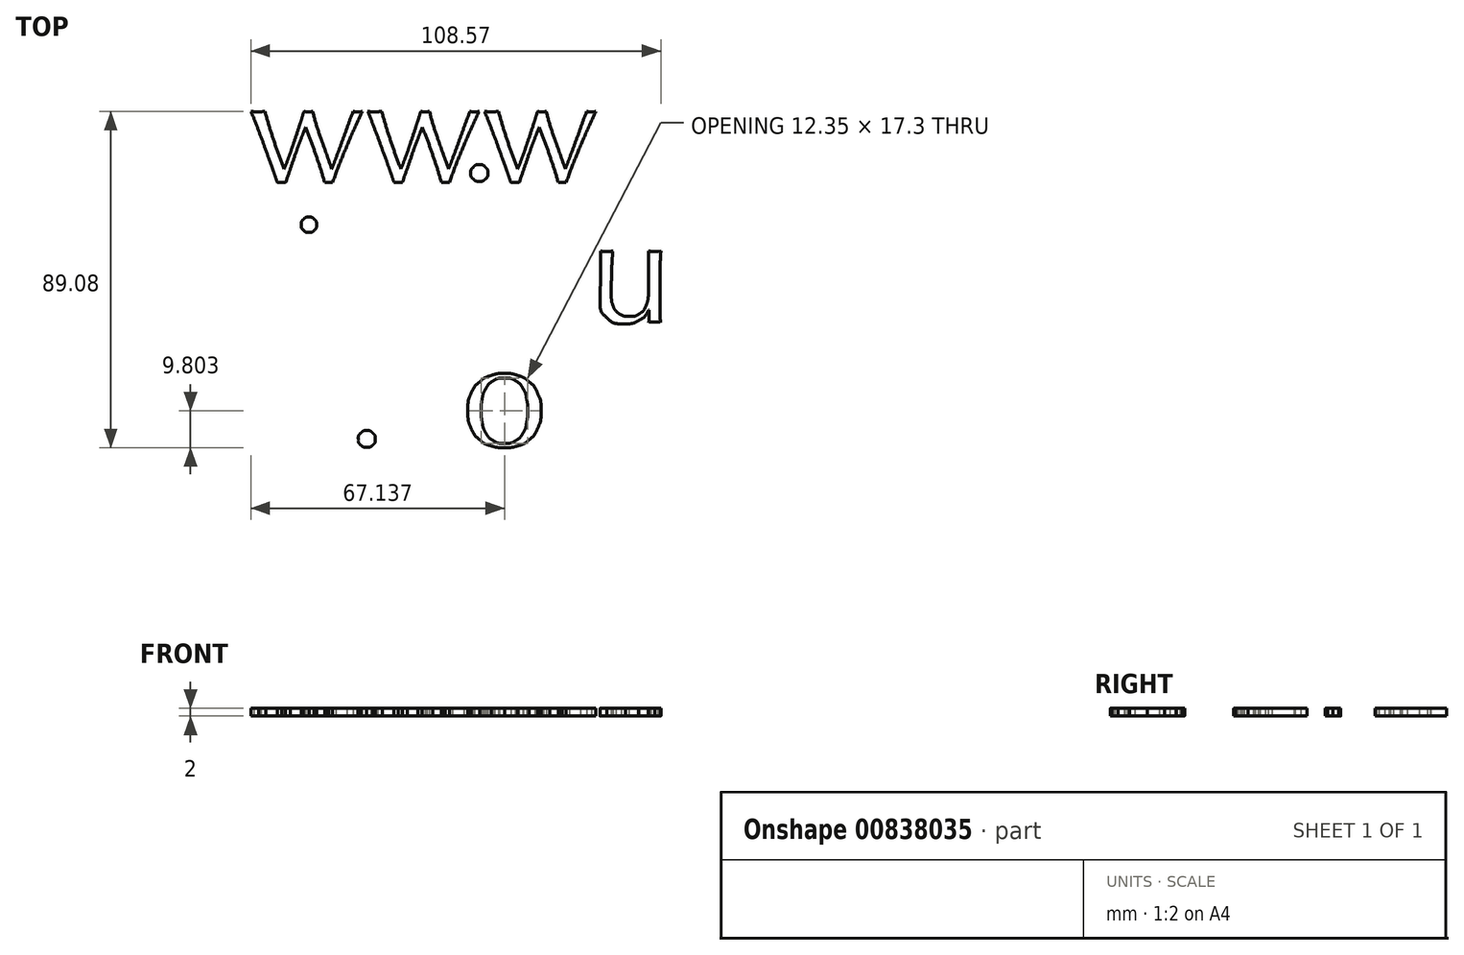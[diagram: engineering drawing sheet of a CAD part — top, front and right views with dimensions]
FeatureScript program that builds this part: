
annotation { "Feature Type Name" : "Feature", "Feature Type Description" : "" }
export const myFeature = defineFeature(function(context is Context, id is Id, definition is map)
    precondition{}
    {
        {
            var Q0;
            Q0=qCreatedBy(makeId("Top.planeOp"),FACE);
            var sketch = newSketch(context, id + "F0", { "sketchPlane" : qUnion([Q0])});
            skLineSegment(sketch, "E0", {"start": v(-60.09, 7.53) * mm, "end": v(-60.57, 7.53) * mm});
            skLineSegment(sketch, "E1", {"start": v(-60.57, 7.53) * mm, "end": v(-60.09, 7.53) * mm});
            skLineSegment(sketch, "E2", {"start": v(-51.53, 19.18) * mm, "end": v(-51.06, 19.18) * mm});
            skLineSegment(sketch, "E3", {"start": v(-51.06, 19.18) * mm, "end": v(-51.53, 19.18) * mm});
            skLineSegment(sketch, "E4", {"start": v(-41, 28.06) * mm, "end": v(-44.3, 26.66) * mm});
            skLineSegment(sketch, "E5", {"start": v(-44.3, 26.66) * mm, "end": v(-41, 28.06) * mm});
            skLineSegment(sketch, "E6", {"start": v(-45.34, 20.7) * mm, "end": v(-44.07, 20.7) * mm});
            skLineSegment(sketch, "E7", {"start": v(-44.07, 20.7) * mm, "end": v(-45.34, 20.7) * mm});
            skLineSegment(sketch, "E8", {"start": v(-36.39, 3.9) * mm, "end": v(-36.39, 4.86) * mm});
            skLineSegment(sketch, "E9", {"start": v(-36.39, 4.86) * mm, "end": v(-36.39, 3.9) * mm});
            skLineSegment(sketch, "E10", {"start": v(-41.12, 20.7) * mm, "end": v(-39.17, 20.7) * mm});
            skLineSegment(sketch, "E11", {"start": v(-39.17, 20.7) * mm, "end": v(-41.12, 20.7) * mm});
            skLineSegment(sketch, "E12", {"start": v(-36.95, 21.02) * mm, "end": v(-36.95, 21.45) * mm});
            skLineSegment(sketch, "E13", {"start": v(-36.95, 21.45) * mm, "end": v(-36.95, 21.85) * mm});
            skLineSegment(sketch, "E14", {"start": v(-36.95, 21.85) * mm, "end": v(-36.95, 21.02) * mm});
            skLineSegment(sketch, "E15", {"start": v(-40.8, 28.06) * mm, "end": v(-41, 28.06) * mm});
            skLineSegment(sketch, "E16", {"start": v(-41, 28.06) * mm, "end": v(-40.8, 28.06) * mm});
            skLineSegment(sketch, "E17", {"start": v(-32.28, 15.29) * mm, "end": v(-32.28, 11.15) * mm});
            skLineSegment(sketch, "E18", {"start": v(-32.28, 11.15) * mm, "end": v(-32.28, 15.29) * mm});
            skLineSegment(sketch, "E19", {"start": v(-29.34, 11.15) * mm, "end": v(-29.34, 15.29) * mm});
            skLineSegment(sketch, "E20", {"start": v(-29.34, 15.29) * mm, "end": v(-29.34, 11.15) * mm});
            skLineSegment(sketch, "E21", {"start": v(-21.25, 22.37) * mm, "end": v(-21.25, 15.17) * mm});
            skLineSegment(sketch, "E22", {"start": v(-21.25, 15.17) * mm, "end": v(-21.25, 22.37) * mm});
            skLineSegment(sketch, "E23", {"start": v(-18.3, 15.17) * mm, "end": v(-18.3, 22.37) * mm});
            skLineSegment(sketch, "E24", {"start": v(-18.3, 22.37) * mm, "end": v(-18.3, 15.17) * mm});
            skLineSegment(sketch, "E25", {"start": v(-10.13, 22.37) * mm, "end": v(-10.13, 15.17) * mm});
            skLineSegment(sketch, "E26", {"start": v(-10.13, 15.17) * mm, "end": v(-10.13, 22.37) * mm});
            skLineSegment(sketch, "E27", {"start": v(-7.19, 15.17) * mm, "end": v(-7.19, 22.37) * mm});
            skLineSegment(sketch, "E28", {"start": v(-7.19, 22.37) * mm, "end": v(-7.19, 15.17) * mm});
            skLineSegment(sketch, "E29", {"start": v(10.17, 13.73) * mm, "end": v(10, 7.77) * mm});
            skLineSegment(sketch, "E30", {"start": v(10, 7.77) * mm, "end": v(10.17, 13.73) * mm});
            skLineSegment(sketch, "E31", {"start": v(0.34, 20.82) * mm, "end": v(0.34, 18.75) * mm});
            skLineSegment(sketch, "E32", {"start": v(0.34, 18.75) * mm, "end": v(0.78, 18.75) * mm});
            skLineSegment(sketch, "E33", {"start": v(0.78, 18.75) * mm, "end": v(0.34, 20.82) * mm});
            skLineSegment(sketch, "E34", {"start": v(15.42, 4.3) * mm, "end": v(15.42, 5.18) * mm});
            skLineSegment(sketch, "E35", {"start": v(15.42, 5.18) * mm, "end": v(15.42, 4.3) * mm});
            skLineSegment(sketch, "E36", {"start": v(19.56, 7.53) * mm, "end": v(19.08, 7.53) * mm});
            skLineSegment(sketch, "E37", {"start": v(19.08, 7.53) * mm, "end": v(19.56, 7.53) * mm});
            skLineSegment(sketch, "E38", {"start": v(28.11, 19.18) * mm, "end": v(28.6, 19.18) * mm});
            skLineSegment(sketch, "E39", {"start": v(28.6, 19.18) * mm, "end": v(28.11, 19.18) * mm});
            skLineSegment(sketch, "E40", {"start": v(38.64, 28.06) * mm, "end": v(35.34, 26.66) * mm});
            skLineSegment(sketch, "E41", {"start": v(35.34, 26.66) * mm, "end": v(38.64, 28.06) * mm});
            skLineSegment(sketch, "E42", {"start": v(34.3, 20.7) * mm, "end": v(35.58, 20.7) * mm});
            skLineSegment(sketch, "E43", {"start": v(35.58, 20.7) * mm, "end": v(34.3, 20.7) * mm});
            skLineSegment(sketch, "E44", {"start": v(43.26, 3.9) * mm, "end": v(43.26, 4.86) * mm});
            skLineSegment(sketch, "E45", {"start": v(43.26, 4.86) * mm, "end": v(43.26, 3.9) * mm});
            skLineSegment(sketch, "E46", {"start": v(38.52, 20.7) * mm, "end": v(40.47, 20.7) * mm});
            skLineSegment(sketch, "E47", {"start": v(40.47, 20.7) * mm, "end": v(38.52, 20.7) * mm});
            skLineSegment(sketch, "E48", {"start": v(42.7, 21.02) * mm, "end": v(42.7, 21.45) * mm});
            skLineSegment(sketch, "E49", {"start": v(42.7, 21.45) * mm, "end": v(42.7, 21.85) * mm});
            skLineSegment(sketch, "E50", {"start": v(42.7, 21.85) * mm, "end": v(42.7, 21.02) * mm});
            skLineSegment(sketch, "E51", {"start": v(38.84, 28.06) * mm, "end": v(38.64, 28.06) * mm});
            skLineSegment(sketch, "E52", {"start": v(38.64, 28.06) * mm, "end": v(38.84, 28.06) * mm});
            skLineSegment(sketch, "E53", {"start": v(59.18, 7.13) * mm, "end": v(59.26, 7.13) * mm});
            skLineSegment(sketch, "E54", {"start": v(59.26, 7.13) * mm, "end": v(59.26, 5.42) * mm});
            skLineSegment(sketch, "E55", {"start": v(59.26, 5.42) * mm, "end": v(59.18, 7.13) * mm});
            skLineSegment(sketch, "E56", {"start": v(59.18, 19.54) * mm, "end": v(59.18, 16.2) * mm});
            skLineSegment(sketch, "E57", {"start": v(59.18, 16.2) * mm, "end": v(59.18, 19.54) * mm});
            skLineSegment(sketch, "E58", {"start": v(-50.25, -25.67) * mm, "end": v(-50.25, -28.1) * mm});
            skLineSegment(sketch, "E59", {"start": v(-50.25, -28.1) * mm, "end": v(-50.25, -25.67) * mm});
            skLineSegment(sketch, "E60", {"start": v(-47.3, -34.42) * mm, "end": v(-47.3, -31.84) * mm});
            skLineSegment(sketch, "E61", {"start": v(-47.3, -31.84) * mm, "end": v(-47.3, -34.42) * mm});
            skLineSegment(sketch, "E62", {"start": v(-59.88, -21.14) * mm, "end": v(-59.96, -21.14) * mm});
            skLineSegment(sketch, "E63", {"start": v(-59.96, -21.14) * mm, "end": v(-59.88, -21.14) * mm});
            skLineSegment(sketch, "E64", {"start": v(-62.9, -25.4) * mm, "end": v(-62.9, -29.53) * mm});
            skLineSegment(sketch, "E65", {"start": v(-62.9, -29.53) * mm, "end": v(-62.9, -25.4) * mm});
            skLineSegment(sketch, "E66", {"start": v(-59.96, -29.53) * mm, "end": v(-59.96, -26.15) * mm});
            skLineSegment(sketch, "E67", {"start": v(-59.96, -26.15) * mm, "end": v(-59.96, -29.53) * mm});
            skLineSegment(sketch, "E68", {"start": v(-27.55, -33.07) * mm, "end": v(-27.67, -36.85) * mm});
            skLineSegment(sketch, "E69", {"start": v(-27.67, -36.85) * mm, "end": v(-27.55, -33.07) * mm});
            skLineSegment(sketch, "E70", {"start": v(-27.67, -17.63) * mm, "end": v(-27.67, -21.53) * mm});
            skLineSegment(sketch, "E71", {"start": v(-27.67, -21.53) * mm, "end": v(-27.75, -21.53) * mm});
            skLineSegment(sketch, "E72", {"start": v(-27.75, -21.53) * mm, "end": v(-27.67, -17.63) * mm});
            skLineSegment(sketch, "E73", {"start": v(-27.63, -33.07) * mm, "end": v(-27.55, -33.07) * mm});
            skLineSegment(sketch, "E74", {"start": v(-27.55, -33.07) * mm, "end": v(-27.63, -33.07) * mm});
            skLineSegment(sketch, "E75", {"start": v(8.25, -25.12) * mm, "end": v(8.05, -25) * mm});
            skLineSegment(sketch, "E76", {"start": v(8.05, -25) * mm, "end": v(8.25, -25.12) * mm});
            skLineSegment(sketch, "E77", {"start": v(7.05, -14.06) * mm, "end": v(7.37, -14.06) * mm});
            skLineSegment(sketch, "E78", {"start": v(7.37, -14.06) * mm, "end": v(7.05, -14.06) * mm});
            skLineSegment(sketch, "E79", {"start": v(35.17, -17.52) * mm, "end": v(35.17, -21.66) * mm});
            skLineSegment(sketch, "E80", {"start": v(35.17, -21.66) * mm, "end": v(35.17, -17.52) * mm});
            skLineSegment(sketch, "E81", {"start": v(38.1, -21.66) * mm, "end": v(38.1, -18.27) * mm});
            skLineSegment(sketch, "E82", {"start": v(38.1, -18.27) * mm, "end": v(38.1, -21.66) * mm});
            skLineSegment(sketch, "E83", {"start": v(49.97, -13.62) * mm, "end": v(49.89, -13.62) * mm});
            skLineSegment(sketch, "E84", {"start": v(49.89, -13.62) * mm, "end": v(49.97, -13.62) * mm});
            skLineSegment(sketch, "E85", {"start": v(38.19, -13.26) * mm, "end": v(38.1, -13.26) * mm});
            skLineSegment(sketch, "E86", {"start": v(38.1, -13.26) * mm, "end": v(38.19, -13.26) * mm});
            skFitSpline(sketch, "E87", {"points": [v(-39.2, 40.8) * mm, v(-38.88, 40.85) * mm, v(-38.5, 40.88) * mm, v(-38.08, 40.88) * mm]});
            skFitSpline(sketch, "E88", {"points": [v(-38.08, 40.88) * mm, v(-37.66, 40.88) * mm, v(-37.28, 40.85) * mm, v(-36.97, 40.8) * mm]});
            skFitSpline(sketch, "E89", {"points": [v(-36.97, 40.8) * mm, v(-36.6, 41.91) * mm, v(-36.17, 43.16) * mm, v(-35.7, 44.54) * mm]});
            skFitSpline(sketch, "E90", {"points": [v(-35.7, 44.54) * mm, v(-35.22, 45.94) * mm, v(-34.74, 47.32) * mm, v(-34.26, 48.67) * mm]});
            skFitSpline(sketch, "E91", {"points": [v(-34.26, 48.67) * mm, v(-33.78, 50.03) * mm, v(-33.32, 51.29) * mm, v(-32.87, 52.45) * mm]});
            skFitSpline(sketch, "E92", {"points": [v(-32.87, 52.45) * mm, v(-32.42, 53.65) * mm, v(-32.03, 54.64) * mm, v(-31.72, 55.44) * mm]});
            skFitSpline(sketch, "E93", {"points": [v(-31.72, 55.44) * mm, v(-30.65, 52.81) * mm, v(-29.71, 50.3) * mm, v(-28.9, 47.92) * mm]});
            skFitSpline(sketch, "E94", {"points": [v(-28.9, 47.92) * mm, v(-28.07, 45.53) * mm, v(-27.31, 43.16) * mm, v(-26.62, 40.8) * mm]});
            skFitSpline(sketch, "E95", {"points": [v(-26.62, 40.8) * mm, v(-26.49, 40.85) * mm, v(-26.33, 40.88) * mm, v(-26.15, 40.88) * mm]});
            skFitSpline(sketch, "E96", {"points": [v(-26.15, 40.88) * mm, v(-25.96, 40.88) * mm, v(-25.77, 40.88) * mm, v(-25.59, 40.88) * mm]});
            skFitSpline(sketch, "E97", {"points": [v(-25.59, 40.88) * mm, v(-25.2, 40.88) * mm, v(-24.85, 40.85) * mm, v(-24.55, 40.8) * mm]});
            skFitSpline(sketch, "E98", {"points": [v(-24.55, 40.8) * mm, v(-23.41, 43.93) * mm, v(-22.2, 47.06) * mm, v(-20.9, 50.19) * mm]});
            skFitSpline(sketch, "E99", {"points": [v(-20.9, 50.19) * mm, v(-19.57, 53.32) * mm, v(-18.15, 56.48) * mm, v(-16.64, 59.7) * mm]});
            skFitSpline(sketch, "E100", {"points": [v(-16.64, 59.7) * mm, v(-17.09, 59.56) * mm, v(-17.49, 59.5) * mm, v(-17.83, 59.5) * mm]});
            skFitSpline(sketch, "E101", {"points": [v(-17.83, 59.5) * mm, v(-18.15, 59.5) * mm, v(-18.57, 59.56) * mm, v(-19.1, 59.7) * mm]});
            skFitSpline(sketch, "E102", {"points": [v(-19.1, 59.7) * mm, v(-19.55, 58.45) * mm, v(-20.04, 57.1) * mm, v(-20.58, 55.68) * mm]});
            skFitSpline(sketch, "E103", {"points": [v(-20.58, 55.68) * mm, v(-21.08, 54.24) * mm, v(-21.58, 52.84) * mm, v(-22.09, 51.46) * mm]});
            skFitSpline(sketch, "E104", {"points": [v(-22.09, 51.46) * mm, v(-22.6, 50.1) * mm, v(-23.08, 48.8) * mm, v(-23.56, 47.56) * mm]});
            skFitSpline(sketch, "E105", {"points": [v(-23.56, 47.56) * mm, v(-24.01, 46.34) * mm, v(-24.4, 45.3) * mm, v(-24.75, 44.46) * mm]});
            skFitSpline(sketch, "E106", {"points": [v(-24.75, 44.46) * mm, v(-25.7, 47.1) * mm, v(-26.62, 49.67) * mm, v(-27.5, 52.13) * mm]});
            skFitSpline(sketch, "E107", {"points": [v(-27.5, 52.13) * mm, v(-28.37, 54.63) * mm, v(-29.14, 57.15) * mm, v(-29.8, 59.7) * mm]});
            skFitSpline(sketch, "E108", {"points": [v(-29.8, 59.7) * mm, v(-30.02, 59.64) * mm, v(-30.2, 59.59) * mm, v(-30.36, 59.53) * mm]});
            skFitSpline(sketch, "E109", {"points": [v(-30.36, 59.53) * mm, v(-30.52, 59.5) * mm, v(-30.7, 59.5) * mm, v(-30.92, 59.5) * mm]});
            skFitSpline(sketch, "E110", {"points": [v(-30.92, 59.5) * mm, v(-31.24, 59.5) * mm, v(-31.64, 59.56) * mm, v(-32.11, 59.7) * mm]});
            skFitSpline(sketch, "E111", {"points": [v(-32.11, 59.7) * mm, v(-32.48, 58.45) * mm, v(-32.9, 57.1) * mm, v(-33.39, 55.64) * mm]});
            skFitSpline(sketch, "E112", {"points": [v(-33.39, 55.64) * mm, v(-33.86, 54.18) * mm, v(-34.34, 52.74) * mm, v(-34.82, 51.34) * mm]});
            skFitSpline(sketch, "E113", {"points": [v(-34.82, 51.34) * mm, v(-35.3, 49.93) * mm, v(-35.76, 48.62) * mm, v(-36.21, 47.4) * mm]});
            skFitSpline(sketch, "E114", {"points": [v(-36.21, 47.4) * mm, v(-36.66, 46.18) * mm, v(-37.05, 45.2) * mm, v(-37.36, 44.46) * mm]});
            skFitSpline(sketch, "E115", {"points": [v(-37.36, 44.46) * mm, v(-38.4, 47.1) * mm, v(-39.34, 49.68) * mm, v(-40.19, 52.17) * mm]});
            skFitSpline(sketch, "E116", {"points": [v(-40.19, 52.17) * mm, v(-41.01, 54.7) * mm, v(-41.77, 57.2) * mm, v(-42.46, 59.7) * mm]});
            skFitSpline(sketch, "E117", {"points": [v(-42.46, 59.7) * mm, v(-42.8, 59.64) * mm, v(-43.12, 59.59) * mm, v(-43.41, 59.53) * mm]});
            skFitSpline(sketch, "E118", {"points": [v(-43.41, 59.53) * mm, v(-43.7, 59.5) * mm, v(-44, 59.5) * mm, v(-44.29, 59.5) * mm]});
            skFitSpline(sketch, "E119", {"points": [v(-44.29, 59.5) * mm, v(-44.6, 59.5) * mm, v(-44.92, 59.5) * mm, v(-45.24, 59.53) * mm]});
            skFitSpline(sketch, "E120", {"points": [v(-45.24, 59.53) * mm, v(-45.53, 59.59) * mm, v(-45.84, 59.64) * mm, v(-46.16, 59.7) * mm]});
            skFitSpline(sketch, "E121", {"points": [v(-46.16, 59.7) * mm, v(-45.5, 58.1) * mm, v(-44.83, 56.4) * mm, v(-44.17, 54.6) * mm]});
            skFitSpline(sketch, "E122", {"points": [v(-44.17, 54.6) * mm, v(-43.48, 52.82) * mm, v(-42.83, 51.07) * mm, v(-42.22, 49.35) * mm]});
            skFitSpline(sketch, "E123", {"points": [v(-42.22, 49.35) * mm, v(-41.58, 47.65) * mm, v(-41, 46.05) * mm, v(-40.47, 44.54) * mm]});
            skFitSpline(sketch, "E124", {"points": [v(-40.47, 44.54) * mm, v(-39.94, 43.02) * mm, v(-39.51, 41.78) * mm, v(-39.2, 40.8) * mm]});
            skFitSpline(sketch, "E125", {"points": [v(-8.27, 40.8) * mm, v(-7.95, 40.85) * mm, v(-7.58, 40.88) * mm, v(-7.15, 40.88) * mm]});
            skFitSpline(sketch, "E126", {"points": [v(-7.15, 40.88) * mm, v(-6.73, 40.88) * mm, v(-6.36, 40.85) * mm, v(-6.04, 40.8) * mm]});
            skFitSpline(sketch, "E127", {"points": [v(-6.04, 40.8) * mm, v(-5.67, 41.91) * mm, v(-5.24, 43.16) * mm, v(-4.77, 44.54) * mm]});
            skFitSpline(sketch, "E128", {"points": [v(-4.77, 44.54) * mm, v(-4.29, 45.94) * mm, v(-3.81, 47.32) * mm, v(-3.33, 48.67) * mm]});
            skFitSpline(sketch, "E129", {"points": [v(-3.33, 48.67) * mm, v(-2.86, 50.03) * mm, v(-2.4, 51.29) * mm, v(-1.94, 52.45) * mm]});
            skFitSpline(sketch, "E130", {"points": [v(-1.94, 52.45) * mm, v(-1.5, 53.65) * mm, v(-1.1, 54.64) * mm, v(-0.79, 55.44) * mm]});
            skFitSpline(sketch, "E131", {"points": [v(-0.79, 55.44) * mm, v(0.27, 52.81) * mm, v(1.21, 50.3) * mm, v(2.04, 47.92) * mm]});
            skFitSpline(sketch, "E132", {"points": [v(2.04, 47.92) * mm, v(2.86, 45.53) * mm, v(3.61, 43.16) * mm, v(4.3, 40.8) * mm]});
            skFitSpline(sketch, "E133", {"points": [v(4.3, 40.8) * mm, v(4.44, 40.85) * mm, v(4.6, 40.88) * mm, v(4.78, 40.88) * mm]});
            skFitSpline(sketch, "E134", {"points": [v(4.78, 40.88) * mm, v(4.97, 40.88) * mm, v(5.15, 40.88) * mm, v(5.34, 40.88) * mm]});
            skFitSpline(sketch, "E135", {"points": [v(5.34, 40.88) * mm, v(5.74, 40.88) * mm, v(6.08, 40.85) * mm, v(6.37, 40.8) * mm]});
            skFitSpline(sketch, "E136", {"points": [v(6.37, 40.8) * mm, v(7.51, 43.93) * mm, v(8.73, 47.06) * mm, v(10.03, 50.19) * mm]});
            skFitSpline(sketch, "E137", {"points": [v(10.03, 50.19) * mm, v(11.36, 53.32) * mm, v(12.78, 56.48) * mm, v(14.3, 59.7) * mm]});
            skFitSpline(sketch, "E138", {"points": [v(14.3, 59.7) * mm, v(13.84, 59.56) * mm, v(13.44, 59.5) * mm, v(13.1, 59.5) * mm]});
            skFitSpline(sketch, "E139", {"points": [v(13.1, 59.5) * mm, v(12.78, 59.5) * mm, v(12.35, 59.56) * mm, v(11.82, 59.7) * mm]});
            skFitSpline(sketch, "E140", {"points": [v(11.82, 59.7) * mm, v(11.37, 58.45) * mm, v(10.88, 57.1) * mm, v(10.35, 55.68) * mm]});
            skFitSpline(sketch, "E141", {"points": [v(10.35, 55.68) * mm, v(9.85, 54.24) * mm, v(9.34, 52.84) * mm, v(8.84, 51.46) * mm]});
            skFitSpline(sketch, "E142", {"points": [v(8.84, 51.46) * mm, v(8.34, 50.1) * mm, v(7.84, 48.8) * mm, v(7.37, 47.56) * mm]});
            skFitSpline(sketch, "E143", {"points": [v(7.37, 47.56) * mm, v(6.92, 46.34) * mm, v(6.52, 45.3) * mm, v(6.17, 44.46) * mm]});
            skFitSpline(sketch, "E144", {"points": [v(6.17, 44.46) * mm, v(5.22, 47.1) * mm, v(4.3, 49.67) * mm, v(3.43, 52.13) * mm]});
            skFitSpline(sketch, "E145", {"points": [v(3.43, 52.13) * mm, v(2.55, 54.63) * mm, v(1.78, 57.15) * mm, v(1.12, 59.7) * mm]});
            skFitSpline(sketch, "E146", {"points": [v(1.12, 59.7) * mm, v(0.9, 59.64) * mm, v(0.72, 59.59) * mm, v(0.56, 59.53) * mm]});
            skFitSpline(sketch, "E147", {"points": [v(0.56, 59.53) * mm, v(0.4, 59.5) * mm, v(0.22, 59.5) * mm, v(0, 59.5) * mm]});
            skFitSpline(sketch, "E148", {"points": [v(0, 59.5) * mm, v(-0.31, 59.5) * mm, v(-0.7, 59.56) * mm, v(-1.19, 59.7) * mm]});
            skFitSpline(sketch, "E149", {"points": [v(-1.19, 59.7) * mm, v(-1.56, 58.45) * mm, v(-1.98, 57.1) * mm, v(-2.46, 55.64) * mm]});
            skFitSpline(sketch, "E150", {"points": [v(-2.46, 55.64) * mm, v(-2.94, 54.18) * mm, v(-3.41, 52.74) * mm, v(-3.9, 51.34) * mm]});
            skFitSpline(sketch, "E151", {"points": [v(-3.9, 51.34) * mm, v(-4.37, 49.93) * mm, v(-4.83, 48.62) * mm, v(-5.28, 47.4) * mm]});
            skFitSpline(sketch, "E152", {"points": [v(-5.28, 47.4) * mm, v(-5.74, 46.18) * mm, v(-6.12, 45.2) * mm, v(-6.44, 44.46) * mm]});
            skFitSpline(sketch, "E153", {"points": [v(-6.44, 44.46) * mm, v(-7.47, 47.1) * mm, v(-8.41, 49.68) * mm, v(-9.26, 52.17) * mm]});
            skFitSpline(sketch, "E154", {"points": [v(-9.26, 52.17) * mm, v(-10.08, 54.7) * mm, v(-10.84, 57.2) * mm, v(-11.53, 59.7) * mm]});
            skFitSpline(sketch, "E155", {"points": [v(-11.53, 59.7) * mm, v(-11.88, 59.64) * mm, v(-12.2, 59.59) * mm, v(-12.49, 59.53) * mm]});
            skFitSpline(sketch, "E156", {"points": [v(-12.49, 59.53) * mm, v(-12.78, 59.5) * mm, v(-13.07, 59.5) * mm, v(-13.36, 59.5) * mm]});
            skFitSpline(sketch, "E157", {"points": [v(-13.36, 59.5) * mm, v(-13.68, 59.5) * mm, v(-14, 59.5) * mm, v(-14.32, 59.53) * mm]});
            skFitSpline(sketch, "E158", {"points": [v(-14.32, 59.53) * mm, v(-14.6, 59.59) * mm, v(-14.91, 59.64) * mm, v(-15.23, 59.7) * mm]});
            skFitSpline(sketch, "E159", {"points": [v(-15.23, 59.7) * mm, v(-14.57, 58.1) * mm, v(-13.9, 56.4) * mm, v(-13.24, 54.6) * mm]});
            skFitSpline(sketch, "E160", {"points": [v(-13.24, 54.6) * mm, v(-12.55, 52.82) * mm, v(-11.9, 51.07) * mm, v(-11.3, 49.35) * mm]});
            skFitSpline(sketch, "E161", {"points": [v(-11.3, 49.35) * mm, v(-10.66, 47.65) * mm, v(-10.07, 46.05) * mm, v(-9.54, 44.54) * mm]});
            skFitSpline(sketch, "E162", {"points": [v(-9.54, 44.54) * mm, v(-9.01, 43.02) * mm, v(-8.59, 41.78) * mm, v(-8.27, 40.8) * mm]});
            skFitSpline(sketch, "E163", {"points": [v(22.66, 40.8) * mm, v(22.98, 40.85) * mm, v(23.35, 40.88) * mm, v(23.77, 40.88) * mm]});
            skFitSpline(sketch, "E164", {"points": [v(23.77, 40.88) * mm, v(24.2, 40.88) * mm, v(24.57, 40.85) * mm, v(24.89, 40.8) * mm]});
            skFitSpline(sketch, "E165", {"points": [v(24.89, 40.8) * mm, v(25.26, 41.91) * mm, v(25.68, 43.16) * mm, v(26.16, 44.54) * mm]});
            skFitSpline(sketch, "E166", {"points": [v(26.16, 44.54) * mm, v(26.64, 45.94) * mm, v(27.11, 47.32) * mm, v(27.6, 48.67) * mm]});
            skFitSpline(sketch, "E167", {"points": [v(27.6, 48.67) * mm, v(28.07, 50.03) * mm, v(28.53, 51.29) * mm, v(28.98, 52.45) * mm]});
            skFitSpline(sketch, "E168", {"points": [v(28.98, 52.45) * mm, v(29.44, 53.65) * mm, v(29.82, 54.64) * mm, v(30.14, 55.44) * mm]});
            skFitSpline(sketch, "E169", {"points": [v(30.14, 55.44) * mm, v(31.2, 52.81) * mm, v(32.14, 50.3) * mm, v(32.96, 47.92) * mm]});
            skFitSpline(sketch, "E170", {"points": [v(32.96, 47.92) * mm, v(33.79, 45.53) * mm, v(34.54, 43.16) * mm, v(35.23, 40.8) * mm]});
            skFitSpline(sketch, "E171", {"points": [v(35.23, 40.8) * mm, v(35.36, 40.85) * mm, v(35.52, 40.88) * mm, v(35.7, 40.88) * mm]});
            skFitSpline(sketch, "E172", {"points": [v(35.7, 40.88) * mm, v(35.9, 40.88) * mm, v(36.08, 40.88) * mm, v(36.27, 40.88) * mm]});
            skFitSpline(sketch, "E173", {"points": [v(36.27, 40.88) * mm, v(36.66, 40.88) * mm, v(37, 40.85) * mm, v(37.3, 40.8) * mm]});
            skFitSpline(sketch, "E174", {"points": [v(37.3, 40.8) * mm, v(38.44, 43.93) * mm, v(39.66, 47.06) * mm, v(40.96, 50.19) * mm]});
            skFitSpline(sketch, "E175", {"points": [v(40.96, 50.19) * mm, v(42.29, 53.32) * mm, v(43.7, 56.48) * mm, v(45.22, 59.7) * mm]});
            skFitSpline(sketch, "E176", {"points": [v(45.22, 59.7) * mm, v(44.77, 59.56) * mm, v(44.37, 59.5) * mm, v(44.02, 59.5) * mm]});
            skFitSpline(sketch, "E177", {"points": [v(44.02, 59.5) * mm, v(43.7, 59.5) * mm, v(43.28, 59.56) * mm, v(42.75, 59.7) * mm]});
            skFitSpline(sketch, "E178", {"points": [v(42.75, 59.7) * mm, v(42.3, 58.45) * mm, v(41.8, 57.1) * mm, v(41.28, 55.68) * mm]});
            skFitSpline(sketch, "E179", {"points": [v(41.28, 55.68) * mm, v(40.77, 54.24) * mm, v(40.27, 52.84) * mm, v(39.77, 51.46) * mm]});
            skFitSpline(sketch, "E180", {"points": [v(39.77, 51.46) * mm, v(39.26, 50.1) * mm, v(38.77, 48.8) * mm, v(38.3, 47.56) * mm]});
            skFitSpline(sketch, "E181", {"points": [v(38.3, 47.56) * mm, v(37.84, 46.34) * mm, v(37.45, 45.3) * mm, v(37.1, 44.46) * mm]});
            skFitSpline(sketch, "E182", {"points": [v(37.1, 44.46) * mm, v(36.15, 47.1) * mm, v(35.23, 49.67) * mm, v(34.36, 52.13) * mm]});
            skFitSpline(sketch, "E183", {"points": [v(34.36, 52.13) * mm, v(33.48, 54.63) * mm, v(32.71, 57.15) * mm, v(32.05, 59.7) * mm]});
            skFitSpline(sketch, "E184", {"points": [v(32.05, 59.7) * mm, v(31.84, 59.64) * mm, v(31.65, 59.59) * mm, v(31.5, 59.53) * mm]});
            skFitSpline(sketch, "E185", {"points": [v(31.5, 59.53) * mm, v(31.33, 59.5) * mm, v(31.15, 59.5) * mm, v(30.93, 59.5) * mm]});
            skFitSpline(sketch, "E186", {"points": [v(30.93, 59.5) * mm, v(30.62, 59.5) * mm, v(30.22, 59.56) * mm, v(29.74, 59.7) * mm]});
            skFitSpline(sketch, "E187", {"points": [v(29.74, 59.7) * mm, v(29.37, 58.45) * mm, v(28.94, 57.1) * mm, v(28.47, 55.64) * mm]});
            skFitSpline(sketch, "E188", {"points": [v(28.47, 55.64) * mm, v(27.99, 54.18) * mm, v(27.51, 52.74) * mm, v(27.03, 51.34) * mm]});
            skFitSpline(sketch, "E189", {"points": [v(27.03, 51.34) * mm, v(26.56, 49.93) * mm, v(26.1, 48.62) * mm, v(25.64, 47.4) * mm]});
            skFitSpline(sketch, "E190", {"points": [v(25.64, 47.4) * mm, v(25.2, 46.18) * mm, v(24.8, 45.2) * mm, v(24.49, 44.46) * mm]});
            skFitSpline(sketch, "E191", {"points": [v(24.49, 44.46) * mm, v(23.45, 47.1) * mm, v(22.51, 49.68) * mm, v(21.66, 52.17) * mm]});
            skFitSpline(sketch, "E192", {"points": [v(21.66, 52.17) * mm, v(20.84, 54.7) * mm, v(20.09, 57.2) * mm, v(19.4, 59.7) * mm]});
            skFitSpline(sketch, "E193", {"points": [v(19.4, 59.7) * mm, v(19.05, 59.64) * mm, v(18.73, 59.59) * mm, v(18.44, 59.53) * mm]});
            skFitSpline(sketch, "E194", {"points": [v(18.44, 59.53) * mm, v(18.15, 59.5) * mm, v(17.86, 59.5) * mm, v(17.57, 59.5) * mm]});
            skFitSpline(sketch, "E195", {"points": [v(17.57, 59.5) * mm, v(17.25, 59.5) * mm, v(16.93, 59.5) * mm, v(16.61, 59.53) * mm]});
            skFitSpline(sketch, "E196", {"points": [v(16.61, 59.53) * mm, v(16.32, 59.59) * mm, v(16.01, 59.64) * mm, v(15.7, 59.7) * mm]});
            skFitSpline(sketch, "E197", {"points": [v(15.7, 59.7) * mm, v(16.36, 58.1) * mm, v(17.02, 56.4) * mm, v(17.69, 54.6) * mm]});
            skFitSpline(sketch, "E198", {"points": [v(17.69, 54.6) * mm, v(18.38, 52.82) * mm, v(19.02, 51.07) * mm, v(19.63, 49.35) * mm]});
            skFitSpline(sketch, "E199", {"points": [v(19.63, 49.35) * mm, v(20.27, 47.65) * mm, v(20.86, 46.05) * mm, v(21.39, 44.54) * mm]});
            skFitSpline(sketch, "E200", {"points": [v(21.39, 44.54) * mm, v(21.92, 43.02) * mm, v(22.34, 41.78) * mm, v(22.66, 40.8) * mm]});
            skFitSpline(sketch, "E201", {"points": [v(12.06, 43.29) * mm, v(12.06, 42.68) * mm, v(12.28, 42.16) * mm, v(12.73, 41.74) * mm]});
            skFitSpline(sketch, "E202", {"points": [v(12.73, 41.74) * mm, v(13.18, 41.34) * mm, v(13.71, 41.14) * mm, v(14.32, 41.14) * mm]});
            skFitSpline(sketch, "E203", {"points": [v(14.32, 41.14) * mm, v(14.93, 41.14) * mm, v(15.46, 41.34) * mm, v(15.91, 41.74) * mm]});
            skFitSpline(sketch, "E204", {"points": [v(15.91, 41.74) * mm, v(16.37, 42.16) * mm, v(16.6, 42.68) * mm, v(16.6, 43.29) * mm]});
            skFitSpline(sketch, "E205", {"points": [v(16.6, 43.29) * mm, v(16.6, 43.9) * mm, v(16.37, 44.43) * mm, v(15.91, 44.88) * mm]});
            skFitSpline(sketch, "E206", {"points": [v(15.91, 44.88) * mm, v(15.46, 45.33) * mm, v(14.93, 45.56) * mm, v(14.32, 45.56) * mm]});
            skFitSpline(sketch, "E207", {"points": [v(14.32, 45.56) * mm, v(13.71, 45.56) * mm, v(13.18, 45.33) * mm, v(12.73, 44.88) * mm]});
            skFitSpline(sketch, "E208", {"points": [v(12.73, 44.88) * mm, v(12.28, 44.43) * mm, v(12.06, 43.9) * mm, v(12.06, 43.29) * mm]});
            skFitSpline(sketch, "E209", {"points": [v(-60.57, 7.53) * mm, v(-60.57, 7.13) * mm, v(-60.66, 6.63) * mm, v(-60.84, 6.02) * mm]});
            skFitSpline(sketch, "E210", {"points": [v(-60.84, 6.02) * mm, v(-61, 5.43) * mm, v(-61.16, 4.97) * mm, v(-61.32, 4.62) * mm]});
            skFitSpline(sketch, "E211", {"points": [v(-61.32, 4.62) * mm, v(-60.76, 4.3) * mm, v(-60.07, 4.03) * mm, v(-59.25, 3.79) * mm]});
            skFitSpline(sketch, "E212", {"points": [v(-59.25, 3.79) * mm, v(-58.43, 3.55) * mm, v(-57.4, 3.43) * mm, v(-56.19, 3.43) * mm]});
            skFitSpline(sketch, "E213", {"points": [v(-56.19, 3.43) * mm, v(-55.08, 3.43) * mm, v(-54.08, 3.59) * mm, v(-53.2, 3.9) * mm]});
            skFitSpline(sketch, "E214", {"points": [v(-53.2, 3.9) * mm, v(-52.33, 4.25) * mm, v(-51.59, 4.72) * mm, v(-50.98, 5.3) * mm]});
            skFitSpline(sketch, "E215", {"points": [v(-50.98, 5.3) * mm, v(-50.34, 5.91) * mm, v(-49.86, 6.59) * mm, v(-49.55, 7.33) * mm]});
            skFitSpline(sketch, "E216", {"points": [v(-49.55, 7.33) * mm, v(-49.2, 8.07) * mm, v(-49.03, 8.83) * mm, v(-49.03, 9.6) * mm]});
            skFitSpline(sketch, "E217", {"points": [v(-49.03, 9.6) * mm, v(-49.03, 10.71) * mm, v(-49.27, 11.59) * mm, v(-49.74, 12.22) * mm]});
            skFitSpline(sketch, "E218", {"points": [v(-49.74, 12.22) * mm, v(-50.2, 12.86) * mm, v(-50.77, 13.35) * mm, v(-51.45, 13.7) * mm]});
            skFitSpline(sketch, "E219", {"points": [v(-51.45, 13.7) * mm, v(-52.14, 14.07) * mm, v(-52.9, 14.34) * mm, v(-53.72, 14.53) * mm]});
            skFitSpline(sketch, "E220", {"points": [v(-53.72, 14.53) * mm, v(-54.54, 14.74) * mm, v(-55.3, 14.98) * mm, v(-56, 15.25) * mm]});
            skFitSpline(sketch, "E221", {"points": [v(-56, 15.25) * mm, v(-56.68, 15.51) * mm, v(-57.26, 15.87) * mm, v(-57.74, 16.32) * mm]});
            skFitSpline(sketch, "E222", {"points": [v(-57.74, 16.32) * mm, v(-58.2, 16.8) * mm, v(-58.42, 17.46) * mm, v(-58.42, 18.3) * mm]});
            skFitSpline(sketch, "E223", {"points": [v(-58.42, 18.3) * mm, v(-58.42, 18.9) * mm, v(-58.31, 19.4) * mm, v(-58.1, 19.82) * mm]});
            skFitSpline(sketch, "E224", {"points": [v(-58.1, 19.82) * mm, v(-57.89, 20.25) * mm, v(-57.62, 20.6) * mm, v(-57.3, 20.86) * mm]});
            skFitSpline(sketch, "E225", {"points": [v(-57.3, 20.86) * mm, v(-56.98, 21.12) * mm, v(-56.63, 21.32) * mm, v(-56.23, 21.45) * mm]});
            skFitSpline(sketch, "E226", {"points": [v(-56.23, 21.45) * mm, v(-55.83, 21.59) * mm, v(-55.43, 21.65) * mm, v(-55.04, 21.65) * mm]});
            skFitSpline(sketch, "E227", {"points": [v(-55.04, 21.65) * mm, v(-54.13, 21.65) * mm, v(-53.38, 21.4) * mm, v(-52.77, 20.9) * mm]});
            skFitSpline(sketch, "E228", {"points": [v(-52.77, 20.9) * mm, v(-52.16, 20.4) * mm, v(-51.75, 19.82) * mm, v(-51.53, 19.18) * mm]});
            skFitSpline(sketch, "E229", {"points": [v(-51.06, 19.18) * mm, v(-51, 19.5) * mm, v(-50.88, 19.95) * mm, v(-50.7, 20.54) * mm]});
            skFitSpline(sketch, "E230", {"points": [v(-50.7, 20.54) * mm, v(-50.51, 21.12) * mm, v(-50.31, 21.61) * mm, v(-50.1, 22) * mm]});
            skFitSpline(sketch, "E231", {"points": [v(-50.1, 22) * mm, v(-50.71, 22.22) * mm, v(-51.36, 22.46) * mm, v(-52.05, 22.73) * mm]});
            skFitSpline(sketch, "E232", {"points": [v(-52.05, 22.73) * mm, v(-52.71, 23) * mm, v(-53.54, 23.12) * mm, v(-54.52, 23.12) * mm]});
            skFitSpline(sketch, "E233", {"points": [v(-54.52, 23.12) * mm, v(-55.58, 23.12) * mm, v(-56.52, 22.96) * mm, v(-57.34, 22.65) * mm]});
            skFitSpline(sketch, "E234", {"points": [v(-57.34, 22.65) * mm, v(-58.17, 22.35) * mm, v(-58.85, 21.94) * mm, v(-59.41, 21.41) * mm]});
            skFitSpline(sketch, "E235", {"points": [v(-59.41, 21.41) * mm, v(-59.97, 20.88) * mm, v(-60.4, 20.25) * mm, v(-60.68, 19.5) * mm]});
            skFitSpline(sketch, "E236", {"points": [v(-60.68, 19.5) * mm, v(-60.98, 18.79) * mm, v(-61.12, 18) * mm, v(-61.12, 17.12) * mm]});
            skFitSpline(sketch, "E237", {"points": [v(-61.12, 17.12) * mm, v(-61.12, 16) * mm, v(-60.9, 15.13) * mm, v(-60.45, 14.5) * mm]});
            skFitSpline(sketch, "E238", {"points": [v(-60.45, 14.5) * mm, v(-59.97, 13.85) * mm, v(-59.39, 13.34) * mm, v(-58.7, 12.94) * mm]});
            skFitSpline(sketch, "E239", {"points": [v(-58.7, 12.94) * mm, v(-58, 12.57) * mm, v(-57.25, 12.28) * mm, v(-56.43, 12.06) * mm]});
            skFitSpline(sketch, "E240", {"points": [v(-56.43, 12.06) * mm, v(-55.6, 11.85) * mm, v(-54.85, 11.6) * mm, v(-54.16, 11.3) * mm]});
            skFitSpline(sketch, "E241", {"points": [v(-54.16, 11.3) * mm, v(-53.47, 11.04) * mm, v(-52.9, 10.68) * mm, v(-52.45, 10.23) * mm]});
            skFitSpline(sketch, "E242", {"points": [v(-52.45, 10.23) * mm, v(-51.97, 9.8) * mm, v(-51.73, 9.19) * mm, v(-51.73, 8.36) * mm]});
            skFitSpline(sketch, "E243", {"points": [v(-51.73, 8.36) * mm, v(-51.73, 7.78) * mm, v(-51.84, 7.26) * mm, v(-52.05, 6.81) * mm]});
            skFitSpline(sketch, "E244", {"points": [v(-52.05, 6.81) * mm, v(-52.26, 6.36) * mm, v(-52.56, 5.99) * mm, v(-52.93, 5.7) * mm]});
            skFitSpline(sketch, "E245", {"points": [v(-52.93, 5.7) * mm, v(-53.27, 5.4) * mm, v(-53.68, 5.18) * mm, v(-54.16, 5.02) * mm]});
            skFitSpline(sketch, "E246", {"points": [v(-54.16, 5.02) * mm, v(-54.61, 4.86) * mm, v(-55.09, 4.78) * mm, v(-55.6, 4.78) * mm]});
            skFitSpline(sketch, "E247", {"points": [v(-55.6, 4.78) * mm, v(-56.15, 4.78) * mm, v(-56.68, 4.88) * mm, v(-57.18, 5.06) * mm]});
            skFitSpline(sketch, "E248", {"points": [v(-57.18, 5.06) * mm, v(-57.66, 5.25) * mm, v(-58.1, 5.47) * mm, v(-58.5, 5.74) * mm]});
            skFitSpline(sketch, "E249", {"points": [v(-58.5, 5.74) * mm, v(-58.87, 6.03) * mm, v(-59.2, 6.33) * mm, v(-59.5, 6.65) * mm]});
            skFitSpline(sketch, "E250", {"points": [v(-59.5, 6.65) * mm, v(-59.76, 6.97) * mm, v(-59.96, 7.26) * mm, v(-60.09, 7.53) * mm]});
            skFitSpline(sketch, "E251", {"points": [v(-44.3, 26.66) * mm, v(-44.25, 25.82) * mm, v(-44.23, 25) * mm, v(-44.23, 24.2) * mm]});
            skFitSpline(sketch, "E252", {"points": [v(-44.23, 24.2) * mm, v(-44.2, 23.4) * mm, v(-44.17, 22.74) * mm, v(-44.15, 22.2) * mm]});
            skFitSpline(sketch, "E253", {"points": [v(-44.15, 22.2) * mm, v(-44.7, 22.2) * mm, v(-45.58, 22.25) * mm, v(-46.77, 22.33) * mm]});
            skFitSpline(sketch, "E254", {"points": [v(-46.77, 22.33) * mm, v(-46.75, 22.2) * mm, v(-46.73, 22.06) * mm, v(-46.73, 21.93) * mm]});
            skFitSpline(sketch, "E255", {"points": [v(-46.73, 21.93) * mm, v(-46.7, 21.8) * mm, v(-46.7, 21.66) * mm, v(-46.7, 21.53) * mm]});
            skFitSpline(sketch, "E256", {"points": [v(-46.7, 21.53) * mm, v(-46.7, 21.37) * mm, v(-46.7, 21.21) * mm, v(-46.73, 21.05) * mm]});
            skFitSpline(sketch, "E257", {"points": [v(-46.73, 21.05) * mm, v(-46.73, 20.92) * mm, v(-46.75, 20.78) * mm, v(-46.77, 20.62) * mm]});
            skFitSpline(sketch, "E258", {"points": [v(-46.77, 20.62) * mm, v(-46.5, 20.64) * mm, v(-46.26, 20.66) * mm, v(-46.02, 20.66) * mm]});
            skFitSpline(sketch, "E259", {"points": [v(-46.02, 20.66) * mm, v(-45.78, 20.68) * mm, v(-45.55, 20.7) * mm, v(-45.34, 20.7) * mm]});
            skFitSpline(sketch, "E260", {"points": [v(-44.07, 20.7) * mm, v(-44.07, 19.21) * mm, v(-44.08, 17.86) * mm, v(-44.1, 16.64) * mm]});
            skFitSpline(sketch, "E261", {"points": [v(-44.1, 16.64) * mm, v(-44.13, 15.45) * mm, v(-44.17, 14.34) * mm, v(-44.23, 13.34) * mm]});
            skFitSpline(sketch, "E262", {"points": [v(-44.23, 13.34) * mm, v(-44.25, 12.36) * mm, v(-44.28, 11.44) * mm, v(-44.3, 10.6) * mm]});
            skFitSpline(sketch, "E263", {"points": [v(-44.3, 10.6) * mm, v(-44.33, 9.77) * mm, v(-44.35, 9) * mm, v(-44.35, 8.28) * mm]});
            skFitSpline(sketch, "E264", {"points": [v(-44.35, 8.28) * mm, v(-44.35, 6.7) * mm, v(-43.95, 5.49) * mm, v(-43.15, 4.66) * mm]});
            skFitSpline(sketch, "E265", {"points": [v(-43.15, 4.66) * mm, v(-42.36, 3.84) * mm, v(-41.12, 3.43) * mm, v(-39.45, 3.43) * mm]});
            skFitSpline(sketch, "E266", {"points": [v(-39.45, 3.43) * mm, v(-38.95, 3.43) * mm, v(-38.43, 3.5) * mm, v(-37.9, 3.63) * mm]});
            skFitSpline(sketch, "E267", {"points": [v(-37.9, 3.63) * mm, v(-37.34, 3.74) * mm, v(-36.84, 3.83) * mm, v(-36.39, 3.9) * mm]});
            skFitSpline(sketch, "E268", {"points": [v(-36.39, 4.86) * mm, v(-36.65, 4.78) * mm, v(-36.97, 4.72) * mm, v(-37.34, 4.66) * mm]});
            skFitSpline(sketch, "E269", {"points": [v(-37.34, 4.66) * mm, v(-37.69, 4.61) * mm, v(-37.97, 4.58) * mm, v(-38.18, 4.58) * mm]});
            skFitSpline(sketch, "E270", {"points": [v(-38.18, 4.58) * mm, v(-38.98, 4.58) * mm, v(-39.59, 4.76) * mm, v(-40, 5.1) * mm]});
            skFitSpline(sketch, "E271", {"points": [v(-40, 5.1) * mm, v(-40.43, 5.45) * mm, v(-40.75, 5.9) * mm, v(-40.96, 6.45) * mm]});
            skFitSpline(sketch, "E272", {"points": [v(-40.96, 6.45) * mm, v(-41.18, 7.04) * mm, v(-41.3, 7.69) * mm, v(-41.36, 8.4) * mm]});
            skFitSpline(sketch, "E273", {"points": [v(-41.36, 8.4) * mm, v(-41.39, 9.12) * mm, v(-41.4, 9.85) * mm, v(-41.4, 10.6) * mm]});
            skFitSpline(sketch, "E274", {"points": [v(-41.4, 10.6) * mm, v(-41.4, 11.47) * mm, v(-41.4, 12.46) * mm, v(-41.4, 13.58) * mm]});
            skFitSpline(sketch, "E275", {"points": [v(-41.4, 13.58) * mm, v(-41.38, 14.69) * mm, v(-41.35, 15.75) * mm, v(-41.32, 16.76) * mm]});
            skFitSpline(sketch, "E276", {"points": [v(-41.32, 16.76) * mm, v(-41.3, 17.8) * mm, v(-41.27, 18.68) * mm, v(-41.24, 19.42) * mm]});
            skFitSpline(sketch, "E277", {"points": [v(-41.24, 19.42) * mm, v(-41.19, 20.17) * mm, v(-41.15, 20.6) * mm, v(-41.12, 20.7) * mm]});
            skFitSpline(sketch, "E278", {"points": [v(-39.17, 20.7) * mm, v(-38.75, 20.7) * mm, v(-38.35, 20.68) * mm, v(-37.98, 20.66) * mm]});
            skFitSpline(sketch, "E279", {"points": [v(-37.98, 20.66) * mm, v(-37.6, 20.66) * mm, v(-37.25, 20.64) * mm, v(-36.9, 20.62) * mm]});
            skFitSpline(sketch, "E280", {"points": [v(-36.9, 20.62) * mm, v(-36.93, 20.7) * mm, v(-36.95, 20.83) * mm, v(-36.95, 21.02) * mm]});
            skFitSpline(sketch, "E281", {"points": [v(-36.95, 21.85) * mm, v(-36.95, 22.06) * mm, v(-36.93, 22.2) * mm, v(-36.9, 22.29) * mm]});
            skFitSpline(sketch, "E282", {"points": [v(-36.9, 22.29) * mm, v(-37.83, 22.24) * mm, v(-38.7, 22.2) * mm, v(-39.5, 22.17) * mm]});
            skFitSpline(sketch, "E283", {"points": [v(-39.5, 22.17) * mm, v(-40.29, 22.17) * mm, v(-40.83, 22.17) * mm, v(-41.12, 22.17) * mm]});
            skFitSpline(sketch, "E284", {"points": [v(-41.12, 22.17) * mm, v(-41.07, 23.15) * mm, v(-41.03, 24.12) * mm, v(-41, 25.07) * mm]});
            skFitSpline(sketch, "E285", {"points": [v(-41, 25.07) * mm, v(-40.95, 26.05) * mm, v(-40.88, 27.05) * mm, v(-40.8, 28.06) * mm]});
            skFitSpline(sketch, "E286", {"points": [v(-32.84, 29.65) * mm, v(-32.84, 29.1) * mm, v(-32.64, 28.61) * mm, v(-32.24, 28.22) * mm]});
            skFitSpline(sketch, "E287", {"points": [v(-32.24, 28.22) * mm, v(-31.84, 27.82) * mm, v(-31.36, 27.62) * mm, v(-30.8, 27.62) * mm]});
            skFitSpline(sketch, "E288", {"points": [v(-30.8, 27.62) * mm, v(-30.25, 27.62) * mm, v(-29.77, 27.82) * mm, v(-29.38, 28.22) * mm]});
            skFitSpline(sketch, "E289", {"points": [v(-29.38, 28.22) * mm, v(-28.98, 28.61) * mm, v(-28.78, 29.1) * mm, v(-28.78, 29.65) * mm]});
            skFitSpline(sketch, "E290", {"points": [v(-28.78, 29.65) * mm, v(-28.78, 30.2) * mm, v(-28.98, 30.68) * mm, v(-29.38, 31.08) * mm]});
            skFitSpline(sketch, "E291", {"points": [v(-29.38, 31.08) * mm, v(-29.77, 31.48) * mm, v(-30.25, 31.68) * mm, v(-30.8, 31.68) * mm]});
            skFitSpline(sketch, "E292", {"points": [v(-30.8, 31.68) * mm, v(-31.36, 31.68) * mm, v(-31.84, 31.48) * mm, v(-32.24, 31.08) * mm]});
            skFitSpline(sketch, "E293", {"points": [v(-32.24, 31.08) * mm, v(-32.64, 30.68) * mm, v(-32.84, 30.2) * mm, v(-32.84, 29.65) * mm]});
            skFitSpline(sketch, "E294", {"points": [v(-32.28, 11.15) * mm, v(-32.28, 9.95) * mm, v(-32.3, 8.7) * mm, v(-32.36, 7.37) * mm]});
            skFitSpline(sketch, "E295", {"points": [v(-32.36, 7.37) * mm, v(-32.39, 6.07) * mm, v(-32.47, 4.89) * mm, v(-32.6, 3.83) * mm]});
            skFitSpline(sketch, "E296", {"points": [v(-32.6, 3.83) * mm, v(-31.99, 3.88) * mm, v(-31.4, 3.9) * mm, v(-30.8, 3.9) * mm]});
            skFitSpline(sketch, "E297", {"points": [v(-30.8, 3.9) * mm, v(-30.22, 3.9) * mm, v(-29.63, 3.88) * mm, v(-29.02, 3.83) * mm]});
            skFitSpline(sketch, "E298", {"points": [v(-29.02, 3.83) * mm, v(-29.15, 4.89) * mm, v(-29.24, 6.07) * mm, v(-29.3, 7.37) * mm]});
            skFitSpline(sketch, "E299", {"points": [v(-29.3, 7.37) * mm, v(-29.32, 8.7) * mm, v(-29.34, 9.95) * mm, v(-29.34, 11.15) * mm]});
            skFitSpline(sketch, "E300", {"points": [v(-29.34, 15.29) * mm, v(-29.34, 16.48) * mm, v(-29.32, 17.73) * mm, v(-29.3, 19.03) * mm]});
            skFitSpline(sketch, "E301", {"points": [v(-29.3, 19.03) * mm, v(-29.24, 20.35) * mm, v(-29.15, 21.59) * mm, v(-29.02, 22.73) * mm]});
            skFitSpline(sketch, "E302", {"points": [v(-29.02, 22.73) * mm, v(-29.76, 22.6) * mm, v(-30.36, 22.53) * mm, v(-30.8, 22.53) * mm]});
            skFitSpline(sketch, "E303", {"points": [v(-30.8, 22.53) * mm, v(-31.26, 22.53) * mm, v(-31.86, 22.6) * mm, v(-32.6, 22.73) * mm]});
            skFitSpline(sketch, "E304", {"points": [v(-32.6, 22.73) * mm, v(-32.47, 21.59) * mm, v(-32.39, 20.35) * mm, v(-32.36, 19.03) * mm]});
            skFitSpline(sketch, "E305", {"points": [v(-32.36, 19.03) * mm, v(-32.3, 17.73) * mm, v(-32.28, 16.48) * mm, v(-32.28, 15.29) * mm]});
            skFitSpline(sketch, "E306", {"points": [v(-21.25, 15.17) * mm, v(-21.25, 14.26) * mm, v(-21.26, 13.28) * mm, v(-21.29, 12.22) * mm]});
            skFitSpline(sketch, "E307", {"points": [v(-21.29, 12.22) * mm, v(-21.29, 11.16) * mm, v(-21.3, 10.11) * mm, v(-21.33, 9.08) * mm]});
            skFitSpline(sketch, "E308", {"points": [v(-21.33, 9.08) * mm, v(-21.35, 8.05) * mm, v(-21.4, 7.06) * mm, v(-21.44, 6.14) * mm]});
            skFitSpline(sketch, "E309", {"points": [v(-21.44, 6.14) * mm, v(-21.47, 5.2) * mm, v(-21.51, 4.44) * mm, v(-21.56, 3.83) * mm]});
            skFitSpline(sketch, "E310", {"points": [v(-21.56, 3.83) * mm, v(-20.95, 3.88) * mm, v(-20.36, 3.9) * mm, v(-19.77, 3.9) * mm]});
            skFitSpline(sketch, "E311", {"points": [v(-19.77, 3.9) * mm, v(-19.19, 3.9) * mm, v(-18.6, 3.88) * mm, v(-17.98, 3.83) * mm]});
            skFitSpline(sketch, "E312", {"points": [v(-17.98, 3.83) * mm, v(-18.04, 4.44) * mm, v(-18.09, 5.2) * mm, v(-18.14, 6.14) * mm]});
            skFitSpline(sketch, "E313", {"points": [v(-18.14, 6.14) * mm, v(-18.17, 7.06) * mm, v(-18.2, 8.05) * mm, v(-18.22, 9.08) * mm]});
            skFitSpline(sketch, "E314", {"points": [v(-18.22, 9.08) * mm, v(-18.25, 10.11) * mm, v(-18.27, 11.16) * mm, v(-18.3, 12.22) * mm]});
            skFitSpline(sketch, "E315", {"points": [v(-18.3, 12.22) * mm, v(-18.3, 13.28) * mm, v(-18.3, 14.26) * mm, v(-18.3, 15.17) * mm]});
            skFitSpline(sketch, "E316", {"points": [v(-18.3, 22.37) * mm, v(-18.3, 23.27) * mm, v(-18.3, 24.25) * mm, v(-18.3, 25.31) * mm]});
            skFitSpline(sketch, "E317", {"points": [v(-18.3, 25.31) * mm, v(-18.27, 26.37) * mm, v(-18.25, 27.42) * mm, v(-18.22, 28.45) * mm]});
            skFitSpline(sketch, "E318", {"points": [v(-18.22, 28.45) * mm, v(-18.2, 29.49) * mm, v(-18.17, 30.47) * mm, v(-18.14, 31.4) * mm]});
            skFitSpline(sketch, "E319", {"points": [v(-18.14, 31.4) * mm, v(-18.09, 32.35) * mm, v(-18.04, 33.16) * mm, v(-17.98, 33.83) * mm]});
            skFitSpline(sketch, "E320", {"points": [v(-17.98, 33.83) * mm, v(-18.73, 33.7) * mm, v(-19.32, 33.63) * mm, v(-19.77, 33.63) * mm]});
            skFitSpline(sketch, "E321", {"points": [v(-19.77, 33.63) * mm, v(-20.22, 33.63) * mm, v(-20.82, 33.7) * mm, v(-21.56, 33.83) * mm]});
            skFitSpline(sketch, "E322", {"points": [v(-21.56, 33.83) * mm, v(-21.51, 33.16) * mm, v(-21.47, 32.35) * mm, v(-21.44, 31.4) * mm]});
            skFitSpline(sketch, "E323", {"points": [v(-21.44, 31.4) * mm, v(-21.4, 30.47) * mm, v(-21.35, 29.49) * mm, v(-21.33, 28.45) * mm]});
            skFitSpline(sketch, "E324", {"points": [v(-21.33, 28.45) * mm, v(-21.3, 27.42) * mm, v(-21.29, 26.37) * mm, v(-21.29, 25.31) * mm]});
            skFitSpline(sketch, "E325", {"points": [v(-21.29, 25.31) * mm, v(-21.26, 24.25) * mm, v(-21.25, 23.27) * mm, v(-21.25, 22.37) * mm]});
            skFitSpline(sketch, "E326", {"points": [v(-10.13, 15.17) * mm, v(-10.13, 14.26) * mm, v(-10.15, 13.28) * mm, v(-10.17, 12.22) * mm]});
            skFitSpline(sketch, "E327", {"points": [v(-10.17, 12.22) * mm, v(-10.17, 11.16) * mm, v(-10.19, 10.11) * mm, v(-10.21, 9.08) * mm]});
            skFitSpline(sketch, "E328", {"points": [v(-10.21, 9.08) * mm, v(-10.24, 8.05) * mm, v(-10.28, 7.06) * mm, v(-10.33, 6.14) * mm]});
            skFitSpline(sketch, "E329", {"points": [v(-10.33, 6.14) * mm, v(-10.36, 5.2) * mm, v(-10.4, 4.44) * mm, v(-10.45, 3.83) * mm]});
            skFitSpline(sketch, "E330", {"points": [v(-10.45, 3.83) * mm, v(-9.84, 3.88) * mm, v(-9.25, 3.9) * mm, v(-8.66, 3.9) * mm]});
            skFitSpline(sketch, "E331", {"points": [v(-8.66, 3.9) * mm, v(-8.08, 3.9) * mm, v(-7.48, 3.88) * mm, v(-6.87, 3.83) * mm]});
            skFitSpline(sketch, "E332", {"points": [v(-6.87, 3.83) * mm, v(-6.92, 4.44) * mm, v(-6.98, 5.2) * mm, v(-7.03, 6.14) * mm]});
            skFitSpline(sketch, "E333", {"points": [v(-7.03, 6.14) * mm, v(-7.06, 7.06) * mm, v(-7.08, 8.05) * mm, v(-7.1, 9.08) * mm]});
            skFitSpline(sketch, "E334", {"points": [v(-7.1, 9.08) * mm, v(-7.14, 10.11) * mm, v(-7.16, 11.16) * mm, v(-7.19, 12.22) * mm]});
            skFitSpline(sketch, "E335", {"points": [v(-7.19, 12.22) * mm, v(-7.19, 13.28) * mm, v(-7.19, 14.26) * mm, v(-7.19, 15.17) * mm]});
            skFitSpline(sketch, "E336", {"points": [v(-7.19, 22.37) * mm, v(-7.19, 23.27) * mm, v(-7.19, 24.25) * mm, v(-7.19, 25.31) * mm]});
            skFitSpline(sketch, "E337", {"points": [v(-7.19, 25.31) * mm, v(-7.16, 26.37) * mm, v(-7.14, 27.42) * mm, v(-7.1, 28.45) * mm]});
            skFitSpline(sketch, "E338", {"points": [v(-7.1, 28.45) * mm, v(-7.08, 29.49) * mm, v(-7.06, 30.47) * mm, v(-7.03, 31.4) * mm]});
            skFitSpline(sketch, "E339", {"points": [v(-7.03, 31.4) * mm, v(-6.98, 32.35) * mm, v(-6.92, 33.16) * mm, v(-6.87, 33.83) * mm]});
            skFitSpline(sketch, "E340", {"points": [v(-6.87, 33.83) * mm, v(-7.61, 33.7) * mm, v(-8.21, 33.63) * mm, v(-8.66, 33.63) * mm]});
            skFitSpline(sketch, "E341", {"points": [v(-8.66, 33.63) * mm, v(-9.11, 33.63) * mm, v(-9.7, 33.7) * mm, v(-10.45, 33.83) * mm]});
            skFitSpline(sketch, "E342", {"points": [v(-10.45, 33.83) * mm, v(-10.4, 33.16) * mm, v(-10.36, 32.35) * mm, v(-10.33, 31.4) * mm]});
            skFitSpline(sketch, "E343", {"points": [v(-10.33, 31.4) * mm, v(-10.28, 30.47) * mm, v(-10.24, 29.49) * mm, v(-10.21, 28.45) * mm]});
            skFitSpline(sketch, "E344", {"points": [v(-10.21, 28.45) * mm, v(-10.19, 27.42) * mm, v(-10.17, 26.37) * mm, v(-10.17, 25.31) * mm]});
            skFitSpline(sketch, "E345", {"points": [v(-10.17, 25.31) * mm, v(-10.15, 24.25) * mm, v(-10.13, 23.27) * mm, v(-10.13, 22.37) * mm]});
            skFitSpline(sketch, "E346", {"points": [v(10, 7.77) * mm, v(9.56, 7.02) * mm, v(8.9, 6.37) * mm, v(8.06, 5.82) * mm]});
            skFitSpline(sketch, "E347", {"points": [v(8.06, 5.82) * mm, v(7.24, 5.26) * mm, v(6.32, 4.98) * mm, v(5.31, 4.98) * mm]});
            skFitSpline(sketch, "E348", {"points": [v(5.31, 4.98) * mm, v(4.44, 4.98) * mm, v(3.64, 5.3) * mm, v(2.93, 5.94) * mm]});
            skFitSpline(sketch, "E349", {"points": [v(2.93, 5.94) * mm, v(2.21, 6.57) * mm, v(1.85, 7.51) * mm, v(1.85, 8.76) * mm]});
            skFitSpline(sketch, "E350", {"points": [v(1.85, 8.76) * mm, v(1.85, 9.5) * mm, v(1.99, 10.11) * mm, v(2.25, 10.6) * mm]});
            skFitSpline(sketch, "E351", {"points": [v(2.25, 10.6) * mm, v(2.54, 11.07) * mm, v(2.91, 11.47) * mm, v(3.37, 11.78) * mm]});
            skFitSpline(sketch, "E352", {"points": [v(3.37, 11.78) * mm, v(3.84, 12.1) * mm, v(4.37, 12.36) * mm, v(4.96, 12.54) * mm]});
            skFitSpline(sketch, "E353", {"points": [v(4.96, 12.54) * mm, v(5.57, 12.73) * mm, v(6.18, 12.87) * mm, v(6.79, 12.98) * mm]});
            skFitSpline(sketch, "E354", {"points": [v(6.79, 12.98) * mm, v(7.4, 13.11) * mm, v(8, 13.23) * mm, v(8.58, 13.34) * mm]});
            skFitSpline(sketch, "E355", {"points": [v(8.58, 13.34) * mm, v(9.19, 13.44) * mm, v(9.72, 13.58) * mm, v(10.17, 13.73) * mm]});
            skFitSpline(sketch, "E356", {"points": [v(0.78, 18.75) * mm, v(1.23, 19.6) * mm, v(1.9, 20.26) * mm, v(2.8, 20.74) * mm]});
            skFitSpline(sketch, "E357", {"points": [v(2.8, 20.74) * mm, v(3.74, 21.21) * mm, v(4.73, 21.45) * mm, v(5.8, 21.45) * mm]});
            skFitSpline(sketch, "E358", {"points": [v(5.8, 21.45) * mm, v(6.59, 21.45) * mm, v(7.26, 21.3) * mm, v(7.82, 21.02) * mm]});
            skFitSpline(sketch, "E359", {"points": [v(7.82, 21.02) * mm, v(8.38, 20.75) * mm, v(8.83, 20.4) * mm, v(9.17, 19.94) * mm]});
            skFitSpline(sketch, "E360", {"points": [v(9.17, 19.94) * mm, v(9.52, 19.49) * mm, v(9.77, 18.96) * mm, v(9.93, 18.35) * mm]});
            skFitSpline(sketch, "E361", {"points": [v(9.93, 18.35) * mm, v(10.09, 17.74) * mm, v(10.17, 17.1) * mm, v(10.17, 16.44) * mm]});
            skFitSpline(sketch, "E362", {"points": [v(10.17, 16.44) * mm, v(10.17, 16.04) * mm, v(10.13, 15.71) * mm, v(10.05, 15.45) * mm]});
            skFitSpline(sketch, "E363", {"points": [v(10.05, 15.45) * mm, v(9.97, 15.2) * mm, v(9.73, 15) * mm, v(9.33, 14.8) * mm]});
            skFitSpline(sketch, "E364", {"points": [v(9.33, 14.8) * mm, v(8.96, 14.62) * mm, v(8.36, 14.44) * mm, v(7.54, 14.25) * mm]});
            skFitSpline(sketch, "E365", {"points": [v(7.54, 14.25) * mm, v(6.75, 14.1) * mm, v(5.63, 13.9) * mm, v(4.2, 13.65) * mm]});
            skFitSpline(sketch, "E366", {"points": [v(4.2, 13.65) * mm, v(2.45, 13.36) * mm, v(1.07, 12.78) * mm, v(0.06, 11.9) * mm]});
            skFitSpline(sketch, "E367", {"points": [v(0.06, 11.9) * mm, v(-0.92, 11.03) * mm, v(-1.4, 9.8) * mm, v(-1.4, 8.2) * mm]});
            skFitSpline(sketch, "E368", {"points": [v(-1.4, 8.2) * mm, v(-1.4, 7.44) * mm, v(-1.26, 6.75) * mm, v(-0.97, 6.14) * mm]});
            skFitSpline(sketch, "E369", {"points": [v(-0.97, 6.14) * mm, v(-0.65, 5.55) * mm, v(-0.26, 5.05) * mm, v(0.22, 4.62) * mm]});
            skFitSpline(sketch, "E370", {"points": [v(0.22, 4.62) * mm, v(0.73, 4.2) * mm, v(1.3, 3.9) * mm, v(1.93, 3.7) * mm]});
            skFitSpline(sketch, "E371", {"points": [v(1.93, 3.7) * mm, v(2.57, 3.52) * mm, v(3.22, 3.43) * mm, v(3.88, 3.43) * mm]});
            skFitSpline(sketch, "E372", {"points": [v(3.88, 3.43) * mm, v(5.24, 3.43) * mm, v(6.38, 3.66) * mm, v(7.3, 4.1) * mm]});
            skFitSpline(sketch, "E373", {"points": [v(7.3, 4.1) * mm, v(8.23, 4.56) * mm, v(9.17, 5.26) * mm, v(10.13, 6.22) * mm]});
            skFitSpline(sketch, "E374", {"points": [v(10.13, 6.22) * mm, v(10.2, 5.53) * mm, v(10.47, 4.96) * mm, v(10.92, 4.5) * mm]});
            skFitSpline(sketch, "E375", {"points": [v(10.92, 4.5) * mm, v(11.38, 4.08) * mm, v(12.03, 3.87) * mm, v(12.87, 3.87) * mm]});
            skFitSpline(sketch, "E376", {"points": [v(12.87, 3.87) * mm, v(13.4, 3.87) * mm, v(13.88, 3.9) * mm, v(14.3, 3.99) * mm]});
            skFitSpline(sketch, "E377", {"points": [v(14.3, 3.99) * mm, v(14.76, 4.07) * mm, v(15.13, 4.17) * mm, v(15.42, 4.3) * mm]});
            skFitSpline(sketch, "E378", {"points": [v(15.42, 5.18) * mm, v(15.29, 5.1) * mm, v(15.14, 5.05) * mm, v(14.98, 5.02) * mm]});
            skFitSpline(sketch, "E379", {"points": [v(14.98, 5.02) * mm, v(14.85, 5.02) * mm, v(14.72, 5.02) * mm, v(14.58, 5.02) * mm]});
            skFitSpline(sketch, "E380", {"points": [v(14.58, 5.02) * mm, v(14.19, 5.02) * mm, v(13.88, 5.11) * mm, v(13.67, 5.3) * mm]});
            skFitSpline(sketch, "E381", {"points": [v(13.67, 5.3) * mm, v(13.48, 5.49) * mm, v(13.34, 5.71) * mm, v(13.23, 5.98) * mm]});
            skFitSpline(sketch, "E382", {"points": [v(13.23, 5.98) * mm, v(13.13, 6.27) * mm, v(13.06, 6.59) * mm, v(13.03, 6.93) * mm]});
            skFitSpline(sketch, "E383", {"points": [v(13.03, 6.93) * mm, v(13.03, 7.3) * mm, v(13.03, 7.65) * mm, v(13.03, 7.97) * mm]});
            skFitSpline(sketch, "E384", {"points": [v(13.03, 7.97) * mm, v(13.03, 9.64) * mm, v(13.06, 11.21) * mm, v(13.11, 12.7) * mm]});
            skFitSpline(sketch, "E385", {"points": [v(13.11, 12.7) * mm, v(13.17, 14.21) * mm, v(13.2, 15.72) * mm, v(13.2, 17.24) * mm]});
            skFitSpline(sketch, "E386", {"points": [v(13.2, 17.24) * mm, v(13.2, 18.11) * mm, v(13.03, 18.9) * mm, v(12.71, 19.62) * mm]});
            skFitSpline(sketch, "E387", {"points": [v(12.71, 19.62) * mm, v(12.4, 20.37) * mm, v(11.96, 20.99) * mm, v(11.4, 21.5) * mm]});
            skFitSpline(sketch, "E388", {"points": [v(11.4, 21.5) * mm, v(10.84, 22.02) * mm, v(10.17, 22.42) * mm, v(9.37, 22.69) * mm]});
            skFitSpline(sketch, "E389", {"points": [v(9.37, 22.69) * mm, v(8.58, 22.98) * mm, v(7.7, 23.12) * mm, v(6.75, 23.12) * mm]});
            skFitSpline(sketch, "E390", {"points": [v(6.75, 23.12) * mm, v(5.69, 23.12) * mm, v(4.65, 22.96) * mm, v(3.64, 22.65) * mm]});
            skFitSpline(sketch, "E391", {"points": [v(3.64, 22.65) * mm, v(2.64, 22.33) * mm, v(1.54, 21.72) * mm, v(0.34, 20.82) * mm]});
            skFitSpline(sketch, "E392", {"points": [v(19.08, 7.53) * mm, v(19.08, 7.13) * mm, v(18.99, 6.63) * mm, v(18.8, 6.02) * mm]});
            skFitSpline(sketch, "E393", {"points": [v(18.8, 6.02) * mm, v(18.64, 5.43) * mm, v(18.49, 4.97) * mm, v(18.33, 4.62) * mm]});
            skFitSpline(sketch, "E394", {"points": [v(18.33, 4.62) * mm, v(18.88, 4.3) * mm, v(19.57, 4.03) * mm, v(20.4, 3.79) * mm]});
            skFitSpline(sketch, "E395", {"points": [v(20.4, 3.79) * mm, v(21.22, 3.55) * mm, v(22.24, 3.43) * mm, v(23.46, 3.43) * mm]});
            skFitSpline(sketch, "E396", {"points": [v(23.46, 3.43) * mm, v(24.57, 3.43) * mm, v(25.57, 3.59) * mm, v(26.44, 3.9) * mm]});
            skFitSpline(sketch, "E397", {"points": [v(26.44, 3.9) * mm, v(27.32, 4.25) * mm, v(28.06, 4.72) * mm, v(28.67, 5.3) * mm]});
            skFitSpline(sketch, "E398", {"points": [v(28.67, 5.3) * mm, v(29.3, 5.91) * mm, v(29.78, 6.59) * mm, v(30.1, 7.33) * mm]});
            skFitSpline(sketch, "E399", {"points": [v(30.1, 7.33) * mm, v(30.45, 8.07) * mm, v(30.62, 8.83) * mm, v(30.62, 9.6) * mm]});
            skFitSpline(sketch, "E400", {"points": [v(30.62, 9.6) * mm, v(30.62, 10.71) * mm, v(30.38, 11.59) * mm, v(29.9, 12.22) * mm]});
            skFitSpline(sketch, "E401", {"points": [v(29.9, 12.22) * mm, v(29.45, 12.86) * mm, v(28.88, 13.35) * mm, v(28.2, 13.7) * mm]});
            skFitSpline(sketch, "E402", {"points": [v(28.2, 13.7) * mm, v(27.5, 14.07) * mm, v(26.75, 14.34) * mm, v(25.93, 14.53) * mm]});
            skFitSpline(sketch, "E403", {"points": [v(25.93, 14.53) * mm, v(25.1, 14.74) * mm, v(24.35, 14.98) * mm, v(23.66, 15.25) * mm]});
            skFitSpline(sketch, "E404", {"points": [v(23.66, 15.25) * mm, v(22.97, 15.51) * mm, v(22.38, 15.87) * mm, v(21.9, 16.32) * mm]});
            skFitSpline(sketch, "E405", {"points": [v(21.9, 16.32) * mm, v(21.46, 16.8) * mm, v(21.23, 17.46) * mm, v(21.23, 18.3) * mm]});
            skFitSpline(sketch, "E406", {"points": [v(21.23, 18.3) * mm, v(21.23, 18.9) * mm, v(21.34, 19.4) * mm, v(21.55, 19.82) * mm]});
            skFitSpline(sketch, "E407", {"points": [v(21.55, 19.82) * mm, v(21.76, 20.25) * mm, v(22.03, 20.6) * mm, v(22.34, 20.86) * mm]});
            skFitSpline(sketch, "E408", {"points": [v(22.34, 20.86) * mm, v(22.66, 21.12) * mm, v(23.02, 21.32) * mm, v(23.42, 21.45) * mm]});
            skFitSpline(sketch, "E409", {"points": [v(23.42, 21.45) * mm, v(23.82, 21.59) * mm, v(24.21, 21.65) * mm, v(24.61, 21.65) * mm]});
            skFitSpline(sketch, "E410", {"points": [v(24.61, 21.65) * mm, v(25.51, 21.65) * mm, v(26.27, 21.4) * mm, v(26.88, 20.9) * mm]});
            skFitSpline(sketch, "E411", {"points": [v(26.88, 20.9) * mm, v(27.5, 20.4) * mm, v(27.9, 19.82) * mm, v(28.11, 19.18) * mm]});
            skFitSpline(sketch, "E412", {"points": [v(28.6, 19.18) * mm, v(28.64, 19.5) * mm, v(28.76, 19.95) * mm, v(28.95, 20.54) * mm]});
            skFitSpline(sketch, "E413", {"points": [v(28.95, 20.54) * mm, v(29.13, 21.12) * mm, v(29.33, 21.61) * mm, v(29.55, 22) * mm]});
            skFitSpline(sketch, "E414", {"points": [v(29.55, 22) * mm, v(28.94, 22.22) * mm, v(28.29, 22.46) * mm, v(27.6, 22.73) * mm]});
            skFitSpline(sketch, "E415", {"points": [v(27.6, 22.73) * mm, v(26.93, 23) * mm, v(26.11, 23.12) * mm, v(25.13, 23.12) * mm]});
            skFitSpline(sketch, "E416", {"points": [v(25.13, 23.12) * mm, v(24.07, 23.12) * mm, v(23.13, 22.96) * mm, v(22.3, 22.65) * mm]});
            skFitSpline(sketch, "E417", {"points": [v(22.3, 22.65) * mm, v(21.48, 22.35) * mm, v(20.8, 21.94) * mm, v(20.24, 21.41) * mm]});
            skFitSpline(sketch, "E418", {"points": [v(20.24, 21.41) * mm, v(19.68, 20.88) * mm, v(19.25, 20.25) * mm, v(18.96, 19.5) * mm]});
            skFitSpline(sketch, "E419", {"points": [v(18.96, 19.5) * mm, v(18.67, 18.79) * mm, v(18.53, 18) * mm, v(18.53, 17.12) * mm]});
            skFitSpline(sketch, "E420", {"points": [v(18.53, 17.12) * mm, v(18.53, 16) * mm, v(18.75, 15.13) * mm, v(19.2, 14.5) * mm]});
            skFitSpline(sketch, "E421", {"points": [v(19.2, 14.5) * mm, v(19.68, 13.85) * mm, v(20.26, 13.34) * mm, v(20.95, 12.94) * mm]});
            skFitSpline(sketch, "E422", {"points": [v(20.95, 12.94) * mm, v(21.64, 12.57) * mm, v(22.4, 12.28) * mm, v(23.22, 12.06) * mm]});
            skFitSpline(sketch, "E423", {"points": [v(23.22, 12.06) * mm, v(24.04, 11.85) * mm, v(24.8, 11.6) * mm, v(25.49, 11.3) * mm]});
            skFitSpline(sketch, "E424", {"points": [v(25.49, 11.3) * mm, v(26.18, 11.04) * mm, v(26.75, 10.68) * mm, v(27.2, 10.23) * mm]});
            skFitSpline(sketch, "E425", {"points": [v(27.2, 10.23) * mm, v(27.68, 9.8) * mm, v(27.91, 9.19) * mm, v(27.91, 8.36) * mm]});
            skFitSpline(sketch, "E426", {"points": [v(27.91, 8.36) * mm, v(27.91, 7.78) * mm, v(27.8, 7.26) * mm, v(27.6, 6.81) * mm]});
            skFitSpline(sketch, "E427", {"points": [v(27.6, 6.81) * mm, v(27.38, 6.36) * mm, v(27.1, 5.99) * mm, v(26.72, 5.7) * mm]});
            skFitSpline(sketch, "E428", {"points": [v(26.72, 5.7) * mm, v(26.38, 5.4) * mm, v(25.96, 5.18) * mm, v(25.49, 5.02) * mm]});
            skFitSpline(sketch, "E429", {"points": [v(25.49, 5.02) * mm, v(25.04, 4.86) * mm, v(24.56, 4.78) * mm, v(24.06, 4.78) * mm]});
            skFitSpline(sketch, "E430", {"points": [v(24.06, 4.78) * mm, v(23.5, 4.78) * mm, v(22.97, 4.88) * mm, v(22.46, 5.06) * mm]});
            skFitSpline(sketch, "E431", {"points": [v(22.46, 5.06) * mm, v(21.99, 5.25) * mm, v(21.55, 5.47) * mm, v(21.15, 5.74) * mm]});
            skFitSpline(sketch, "E432", {"points": [v(21.15, 5.74) * mm, v(20.78, 6.03) * mm, v(20.45, 6.33) * mm, v(20.16, 6.65) * mm]});
            skFitSpline(sketch, "E433", {"points": [v(20.16, 6.65) * mm, v(19.9, 6.97) * mm, v(19.7, 7.26) * mm, v(19.56, 7.53) * mm]});
            skFitSpline(sketch, "E434", {"points": [v(35.34, 26.66) * mm, v(35.4, 25.82) * mm, v(35.42, 25) * mm, v(35.42, 24.2) * mm]});
            skFitSpline(sketch, "E435", {"points": [v(35.42, 24.2) * mm, v(35.45, 23.4) * mm, v(35.47, 22.74) * mm, v(35.5, 22.2) * mm]});
            skFitSpline(sketch, "E436", {"points": [v(35.5, 22.2) * mm, v(34.94, 22.2) * mm, v(34.07, 22.25) * mm, v(32.87, 22.33) * mm]});
            skFitSpline(sketch, "E437", {"points": [v(32.87, 22.33) * mm, v(32.9, 22.2) * mm, v(32.91, 22.06) * mm, v(32.91, 21.93) * mm]});
            skFitSpline(sketch, "E438", {"points": [v(32.91, 21.93) * mm, v(32.94, 21.8) * mm, v(32.95, 21.66) * mm, v(32.95, 21.53) * mm]});
            skFitSpline(sketch, "E439", {"points": [v(32.95, 21.53) * mm, v(32.95, 21.37) * mm, v(32.94, 21.21) * mm, v(32.91, 21.05) * mm]});
            skFitSpline(sketch, "E440", {"points": [v(32.91, 21.05) * mm, v(32.91, 20.92) * mm, v(32.9, 20.78) * mm, v(32.87, 20.62) * mm]});
            skFitSpline(sketch, "E441", {"points": [v(32.87, 20.62) * mm, v(33.14, 20.64) * mm, v(33.4, 20.66) * mm, v(33.63, 20.66) * mm]});
            skFitSpline(sketch, "E442", {"points": [v(33.63, 20.66) * mm, v(33.87, 20.68) * mm, v(34.1, 20.7) * mm, v(34.3, 20.7) * mm]});
            skFitSpline(sketch, "E443", {"points": [v(35.58, 20.7) * mm, v(35.58, 19.21) * mm, v(35.57, 17.86) * mm, v(35.54, 16.64) * mm]});
            skFitSpline(sketch, "E444", {"points": [v(35.54, 16.64) * mm, v(35.51, 15.45) * mm, v(35.47, 14.34) * mm, v(35.42, 13.34) * mm]});
            skFitSpline(sketch, "E445", {"points": [v(35.42, 13.34) * mm, v(35.4, 12.36) * mm, v(35.37, 11.44) * mm, v(35.34, 10.6) * mm]});
            skFitSpline(sketch, "E446", {"points": [v(35.34, 10.6) * mm, v(35.31, 9.77) * mm, v(35.3, 9) * mm, v(35.3, 8.28) * mm]});
            skFitSpline(sketch, "E447", {"points": [v(35.3, 8.28) * mm, v(35.3, 6.7) * mm, v(35.7, 5.49) * mm, v(36.5, 4.66) * mm]});
            skFitSpline(sketch, "E448", {"points": [v(36.5, 4.66) * mm, v(37.3, 3.84) * mm, v(38.52, 3.43) * mm, v(40.2, 3.43) * mm]});
            skFitSpline(sketch, "E449", {"points": [v(40.2, 3.43) * mm, v(40.7, 3.43) * mm, v(41.22, 3.5) * mm, v(41.75, 3.63) * mm]});
            skFitSpline(sketch, "E450", {"points": [v(41.75, 3.63) * mm, v(42.3, 3.74) * mm, v(42.8, 3.83) * mm, v(43.26, 3.9) * mm]});
            skFitSpline(sketch, "E451", {"points": [v(43.26, 4.86) * mm, v(43, 4.78) * mm, v(42.67, 4.72) * mm, v(42.3, 4.66) * mm]});
            skFitSpline(sketch, "E452", {"points": [v(42.3, 4.66) * mm, v(41.96, 4.61) * mm, v(41.68, 4.58) * mm, v(41.47, 4.58) * mm]});
            skFitSpline(sketch, "E453", {"points": [v(41.47, 4.58) * mm, v(40.67, 4.58) * mm, v(40.06, 4.76) * mm, v(39.64, 5.1) * mm]});
            skFitSpline(sketch, "E454", {"points": [v(39.64, 5.1) * mm, v(39.21, 5.45) * mm, v(38.9, 5.9) * mm, v(38.68, 6.45) * mm]});
            skFitSpline(sketch, "E455", {"points": [v(38.68, 6.45) * mm, v(38.47, 7.04) * mm, v(38.34, 7.69) * mm, v(38.29, 8.4) * mm]});
            skFitSpline(sketch, "E456", {"points": [v(38.29, 8.4) * mm, v(38.26, 9.12) * mm, v(38.25, 9.85) * mm, v(38.25, 10.6) * mm]});
            skFitSpline(sketch, "E457", {"points": [v(38.25, 10.6) * mm, v(38.25, 11.47) * mm, v(38.25, 12.46) * mm, v(38.25, 13.58) * mm]});
            skFitSpline(sketch, "E458", {"points": [v(38.25, 13.58) * mm, v(38.27, 14.69) * mm, v(38.3, 15.75) * mm, v(38.33, 16.76) * mm]});
            skFitSpline(sketch, "E459", {"points": [v(38.33, 16.76) * mm, v(38.35, 17.8) * mm, v(38.38, 18.68) * mm, v(38.4, 19.42) * mm]});
            skFitSpline(sketch, "E460", {"points": [v(38.4, 19.42) * mm, v(38.46, 20.17) * mm, v(38.5, 20.6) * mm, v(38.52, 20.7) * mm]});
            skFitSpline(sketch, "E461", {"points": [v(40.47, 20.7) * mm, v(40.9, 20.7) * mm, v(41.3, 20.68) * mm, v(41.67, 20.66) * mm]});
            skFitSpline(sketch, "E462", {"points": [v(41.67, 20.66) * mm, v(42.04, 20.66) * mm, v(42.4, 20.64) * mm, v(42.74, 20.62) * mm]});
            skFitSpline(sketch, "E463", {"points": [v(42.74, 20.62) * mm, v(42.71, 20.7) * mm, v(42.7, 20.83) * mm, v(42.7, 21.02) * mm]});
            skFitSpline(sketch, "E464", {"points": [v(42.7, 21.85) * mm, v(42.7, 22.06) * mm, v(42.71, 22.2) * mm, v(42.74, 22.29) * mm]});
            skFitSpline(sketch, "E465", {"points": [v(42.74, 22.29) * mm, v(41.81, 22.24) * mm, v(40.95, 22.2) * mm, v(40.16, 22.17) * mm]});
            skFitSpline(sketch, "E466", {"points": [v(40.16, 22.17) * mm, v(39.36, 22.17) * mm, v(38.82, 22.17) * mm, v(38.52, 22.17) * mm]});
            skFitSpline(sketch, "E467", {"points": [v(38.52, 22.17) * mm, v(38.58, 23.15) * mm, v(38.62, 24.12) * mm, v(38.64, 25.07) * mm]});
            skFitSpline(sketch, "E468", {"points": [v(38.64, 25.07) * mm, v(38.7, 26.05) * mm, v(38.76, 27.05) * mm, v(38.84, 28.06) * mm]});
            skFitSpline(sketch, "E469", {"points": [v(46.33, 9.84) * mm, v(46.33, 7.77) * mm, v(46.92, 6.18) * mm, v(48.08, 5.06) * mm]});
            skFitSpline(sketch, "E470", {"points": [v(48.08, 5.06) * mm, v(49.28, 3.97) * mm, v(50.9, 3.43) * mm, v(52.98, 3.43) * mm]});
            skFitSpline(sketch, "E471", {"points": [v(52.98, 3.43) * mm, v(54.25, 3.43) * mm, v(55.43, 3.72) * mm, v(56.52, 4.3) * mm]});
            skFitSpline(sketch, "E472", {"points": [v(56.52, 4.3) * mm, v(57.6, 4.92) * mm, v(58.5, 5.86) * mm, v(59.18, 7.13) * mm]});
            skFitSpline(sketch, "E473", {"points": [v(59.26, 5.42) * mm, v(59.26, 5.13) * mm, v(59.25, 4.85) * mm, v(59.22, 4.58) * mm]});
            skFitSpline(sketch, "E474", {"points": [v(59.22, 4.58) * mm, v(59.22, 4.32) * mm, v(59.21, 4.07) * mm, v(59.18, 3.83) * mm]});
            skFitSpline(sketch, "E475", {"points": [v(59.18, 3.83) * mm, v(59.71, 3.88) * mm, v(60.23, 3.9) * mm, v(60.74, 3.9) * mm]});
            skFitSpline(sketch, "E476", {"points": [v(60.74, 3.9) * mm, v(61.24, 3.9) * mm, v(61.76, 3.88) * mm, v(62.29, 3.83) * mm]});
            skFitSpline(sketch, "E477", {"points": [v(62.29, 3.83) * mm, v(62.23, 4.89) * mm, v(62.2, 5.99) * mm, v(62.17, 7.13) * mm]});
            skFitSpline(sketch, "E478", {"points": [v(62.17, 7.13) * mm, v(62.14, 8.27) * mm, v(62.13, 9.44) * mm, v(62.13, 10.63) * mm]});
            skFitSpline(sketch, "E479", {"points": [v(62.13, 10.63) * mm, v(62.13, 12.78) * mm, v(62.14, 14.8) * mm, v(62.17, 16.72) * mm]});
            skFitSpline(sketch, "E480", {"points": [v(62.17, 16.72) * mm, v(62.2, 18.65) * mm, v(62.27, 20.66) * mm, v(62.4, 22.73) * mm]});
            skFitSpline(sketch, "E481", {"points": [v(62.4, 22.73) * mm, v(62.14, 22.67) * mm, v(61.88, 22.62) * mm, v(61.61, 22.57) * mm]});
            skFitSpline(sketch, "E482", {"points": [v(61.61, 22.57) * mm, v(61.35, 22.54) * mm, v(61.07, 22.53) * mm, v(60.78, 22.53) * mm]});
            skFitSpline(sketch, "E483", {"points": [v(60.78, 22.53) * mm, v(60.48, 22.53) * mm, v(60.2, 22.54) * mm, v(59.94, 22.57) * mm]});
            skFitSpline(sketch, "E484", {"points": [v(59.94, 22.57) * mm, v(59.67, 22.62) * mm, v(59.4, 22.67) * mm, v(59.1, 22.73) * mm]});
            skFitSpline(sketch, "E485", {"points": [v(59.1, 22.73) * mm, v(59.13, 22.25) * mm, v(59.14, 21.74) * mm, v(59.14, 21.21) * mm]});
            skFitSpline(sketch, "E486", {"points": [v(59.14, 21.21) * mm, v(59.17, 20.68) * mm, v(59.18, 20.13) * mm, v(59.18, 19.54) * mm]});
            skFitSpline(sketch, "E487", {"points": [v(59.18, 16.2) * mm, v(59.18, 14.64) * mm, v(59.17, 13.4) * mm, v(59.14, 12.5) * mm]});
            skFitSpline(sketch, "E488", {"points": [v(59.14, 12.5) * mm, v(59.14, 11.6) * mm, v(59.1, 10.88) * mm, v(59.03, 10.35) * mm]});
            skFitSpline(sketch, "E489", {"points": [v(59.03, 10.35) * mm, v(58.97, 9.82) * mm, v(58.9, 9.4) * mm, v(58.79, 9.08) * mm]});
            skFitSpline(sketch, "E490", {"points": [v(58.79, 9.08) * mm, v(58.68, 8.76) * mm, v(58.53, 8.38) * mm, v(58.35, 7.93) * mm]});
            skFitSpline(sketch, "E491", {"points": [v(58.35, 7.93) * mm, v(58, 7.2) * mm, v(57.46, 6.6) * mm, v(56.72, 6.1) * mm]});
            skFitSpline(sketch, "E492", {"points": [v(56.72, 6.1) * mm, v(55.97, 5.62) * mm, v(55.05, 5.38) * mm, v(53.93, 5.38) * mm]});
            skFitSpline(sketch, "E493", {"points": [v(53.93, 5.38) * mm, v(53.16, 5.38) * mm, v(52.49, 5.51) * mm, v(51.9, 5.78) * mm]});
            skFitSpline(sketch, "E494", {"points": [v(51.9, 5.78) * mm, v(51.35, 6.07) * mm, v(50.88, 6.43) * mm, v(50.51, 6.85) * mm]});
            skFitSpline(sketch, "E495", {"points": [v(50.51, 6.85) * mm, v(50.17, 7.22) * mm, v(49.87, 7.77) * mm, v(49.64, 8.48) * mm]});
            skFitSpline(sketch, "E496", {"points": [v(49.64, 8.48) * mm, v(49.4, 9.23) * mm, v(49.28, 10.29) * mm, v(49.28, 11.67) * mm]});
            skFitSpline(sketch, "E497", {"points": [v(49.28, 11.67) * mm, v(49.28, 13.65) * mm, v(49.3, 15.6) * mm, v(49.36, 17.47) * mm]});
            skFitSpline(sketch, "E498", {"points": [v(49.36, 17.47) * mm, v(49.44, 19.38) * mm, v(49.54, 21.13) * mm, v(49.68, 22.73) * mm]});
            skFitSpline(sketch, "E499", {"points": [v(49.68, 22.73) * mm, v(49.01, 22.6) * mm, v(48.47, 22.53) * mm, v(48.04, 22.53) * mm]});
            skFitSpline(sketch, "E500", {"points": [v(48.04, 22.53) * mm, v(47.6, 22.53) * mm, v(47.04, 22.6) * mm, v(46.37, 22.73) * mm]});
            skFitSpline(sketch, "E501", {"points": [v(46.37, 22.73) * mm, v(46.4, 21.61) * mm, v(46.41, 20.51) * mm, v(46.41, 19.42) * mm]});
            skFitSpline(sketch, "E502", {"points": [v(46.41, 19.42) * mm, v(46.44, 18.34) * mm, v(46.45, 17.33) * mm, v(46.45, 16.4) * mm]});
            skFitSpline(sketch, "E503", {"points": [v(46.45, 16.4) * mm, v(46.45, 15.42) * mm, v(46.43, 14.42) * mm, v(46.37, 13.42) * mm]});
            skFitSpline(sketch, "E504", {"points": [v(46.37, 13.42) * mm, v(46.35, 12.43) * mm, v(46.33, 11.24) * mm, v(46.33, 9.84) * mm]});
            skFitSpline(sketch, "E505", {"points": [v(-50.25, -28.1) * mm, v(-50.25, -29.64) * mm, v(-50.3, -31.13) * mm, v(-50.37, -32.6) * mm]});
            skFitSpline(sketch, "E506", {"points": [v(-50.37, -32.6) * mm, v(-50.42, -34.05) * mm, v(-50.48, -35.47) * mm, v(-50.53, -36.85) * mm]});
            skFitSpline(sketch, "E507", {"points": [v(-50.53, -36.85) * mm, v(-50, -36.8) * mm, v(-49.46, -36.77) * mm, v(-48.9, -36.77) * mm]});
            skFitSpline(sketch, "E508", {"points": [v(-48.9, -36.77) * mm, v(-48.32, -36.77) * mm, v(-47.76, -36.8) * mm, v(-47.23, -36.85) * mm]});
            skFitSpline(sketch, "E509", {"points": [v(-47.23, -36.85) * mm, v(-47.25, -36.48) * mm, v(-47.28, -36.1) * mm, v(-47.3, -35.7) * mm]});
            skFitSpline(sketch, "E510", {"points": [v(-47.3, -35.7) * mm, v(-47.3, -35.27) * mm, v(-47.3, -34.85) * mm, v(-47.3, -34.42) * mm]});
            skFitSpline(sketch, "E511", {"points": [v(-47.3, -31.84) * mm, v(-47.3, -30.49) * mm, v(-47.28, -29.21) * mm, v(-47.23, -28.02) * mm]});
            skFitSpline(sketch, "E512", {"points": [v(-47.23, -28.02) * mm, v(-47.18, -26.8) * mm, v(-47.15, -25.62) * mm, v(-47.15, -24.48) * mm]});
            skFitSpline(sketch, "E513", {"points": [v(-47.15, -24.48) * mm, v(-47.15, -23.1) * mm, v(-47.35, -21.97) * mm, v(-47.75, -21.1) * mm]});
            skFitSpline(sketch, "E514", {"points": [v(-47.75, -21.1) * mm, v(-48.12, -20.2) * mm, v(-48.6, -19.5) * mm, v(-49.22, -18.99) * mm]});
            skFitSpline(sketch, "E515", {"points": [v(-49.22, -18.99) * mm, v(-49.83, -18.46) * mm, v(-50.52, -18.09) * mm, v(-51.29, -17.87) * mm]});
            skFitSpline(sketch, "E516", {"points": [v(-51.29, -17.87) * mm, v(-52.03, -17.66) * mm, v(-52.77, -17.55) * mm, v(-53.51, -17.55) * mm]});
            skFitSpline(sketch, "E517", {"points": [v(-53.51, -17.55) * mm, v(-54.95, -17.55) * mm, v(-56.18, -17.87) * mm, v(-57.21, -18.5) * mm]});
            skFitSpline(sketch, "E518", {"points": [v(-57.21, -18.5) * mm, v(-58.25, -19.12) * mm, v(-59.14, -20) * mm, v(-59.88, -21.14) * mm]});
            skFitSpline(sketch, "E519", {"points": [v(-59.96, -21.14) * mm, v(-59.96, -20.07) * mm, v(-59.92, -19.01) * mm, v(-59.84, -17.95) * mm]});
            skFitSpline(sketch, "E520", {"points": [v(-59.84, -17.95) * mm, v(-60.18, -18) * mm, v(-60.49, -18.06) * mm, v(-60.76, -18.11) * mm]});
            skFitSpline(sketch, "E521", {"points": [v(-60.76, -18.11) * mm, v(-61, -18.14) * mm, v(-61.22, -18.15) * mm, v(-61.43, -18.15) * mm]});
            skFitSpline(sketch, "E522", {"points": [v(-61.43, -18.15) * mm, v(-61.88, -18.15) * mm, v(-62.48, -18.09) * mm, v(-63.22, -17.95) * mm]});
            skFitSpline(sketch, "E523", {"points": [v(-63.22, -17.95) * mm, v(-63.09, -19.1) * mm, v(-63, -20.33) * mm, v(-62.98, -21.65) * mm]});
            skFitSpline(sketch, "E524", {"points": [v(-62.98, -21.65) * mm, v(-62.93, -22.95) * mm, v(-62.9, -24.2) * mm, v(-62.9, -25.4) * mm]});
            skFitSpline(sketch, "E525", {"points": [v(-62.9, -29.53) * mm, v(-62.9, -30.72) * mm, v(-62.93, -31.98) * mm, v(-62.98, -33.3) * mm]});
            skFitSpline(sketch, "E526", {"points": [v(-62.98, -33.3) * mm, v(-63, -34.6) * mm, v(-63.09, -35.79) * mm, v(-63.22, -36.85) * mm]});
            skFitSpline(sketch, "E527", {"points": [v(-63.22, -36.85) * mm, v(-62.61, -36.8) * mm, v(-62.02, -36.77) * mm, v(-61.43, -36.77) * mm]});
            skFitSpline(sketch, "E528", {"points": [v(-61.43, -36.77) * mm, v(-60.85, -36.77) * mm, v(-60.25, -36.8) * mm, v(-59.64, -36.85) * mm]});
            skFitSpline(sketch, "E529", {"points": [v(-59.64, -36.85) * mm, v(-59.77, -35.79) * mm, v(-59.87, -34.6) * mm, v(-59.92, -33.3) * mm]});
            skFitSpline(sketch, "E530", {"points": [v(-59.92, -33.3) * mm, v(-59.95, -31.98) * mm, v(-59.96, -30.72) * mm, v(-59.96, -29.53) * mm]});
            skFitSpline(sketch, "E531", {"points": [v(-59.96, -26.15) * mm, v(-59.96, -24.08) * mm, v(-59.54, -22.48) * mm, v(-58.69, -21.33) * mm]});
            skFitSpline(sketch, "E532", {"points": [v(-58.69, -21.33) * mm, v(-57.81, -20.2) * mm, v(-56.45, -19.62) * mm, v(-54.59, -19.62) * mm]});
            skFitSpline(sketch, "E533", {"points": [v(-54.59, -19.62) * mm, v(-53.24, -19.62) * mm, v(-52.17, -20.14) * mm, v(-51.4, -21.18) * mm]});
            skFitSpline(sketch, "E534", {"points": [v(-51.4, -21.18) * mm, v(-50.64, -22.18) * mm, v(-50.25, -23.68) * mm, v(-50.25, -25.67) * mm]});
            skFitSpline(sketch, "E535", {"points": [v(-38.93, -27.82) * mm, v(-38.93, -26.63) * mm, v(-38.82, -25.51) * mm, v(-38.6, -24.48) * mm]});
            skFitSpline(sketch, "E536", {"points": [v(-38.6, -24.48) * mm, v(-38.37, -23.42) * mm, v(-38.03, -22.5) * mm, v(-37.57, -21.73) * mm]});
            skFitSpline(sketch, "E537", {"points": [v(-37.57, -21.73) * mm, v(-37.1, -20.94) * mm, v(-36.51, -20.33) * mm, v(-35.82, -19.9) * mm]});
            skFitSpline(sketch, "E538", {"points": [v(-35.82, -19.9) * mm, v(-35.1, -19.45) * mm, v(-34.27, -19.23) * mm, v(-33.32, -19.23) * mm]});
            skFitSpline(sketch, "E539", {"points": [v(-33.32, -19.23) * mm, v(-31.4, -19.23) * mm, v(-29.96, -19.9) * mm, v(-28.98, -21.25) * mm]});
            skFitSpline(sketch, "E540", {"points": [v(-28.98, -21.25) * mm, v(-28, -22.58) * mm, v(-27.5, -24.52) * mm, v(-27.5, -27.06) * mm]});
            skFitSpline(sketch, "E541", {"points": [v(-27.5, -27.06) * mm, v(-27.5, -28.12) * mm, v(-27.63, -29.19) * mm, v(-27.87, -30.25) * mm]});
            skFitSpline(sketch, "E542", {"points": [v(-27.87, -30.25) * mm, v(-28.08, -31.3) * mm, v(-28.44, -32.26) * mm, v(-28.94, -33.11) * mm]});
            skFitSpline(sketch, "E543", {"points": [v(-28.94, -33.11) * mm, v(-29.42, -33.93) * mm, v(-30.03, -34.6) * mm, v(-30.77, -35.14) * mm]});
            skFitSpline(sketch, "E544", {"points": [v(-30.77, -35.14) * mm, v(-31.51, -35.64) * mm, v(-32.4, -35.9) * mm, v(-33.44, -35.9) * mm]});
            skFitSpline(sketch, "E545", {"points": [v(-33.44, -35.9) * mm, v(-34.07, -35.9) * mm, v(-34.72, -35.78) * mm, v(-35.39, -35.54) * mm]});
            skFitSpline(sketch, "E546", {"points": [v(-35.39, -35.54) * mm, v(-36.05, -35.3) * mm, v(-36.65, -34.87) * mm, v(-37.18, -34.26) * mm]});
            skFitSpline(sketch, "E547", {"points": [v(-37.18, -34.26) * mm, v(-37.68, -33.63) * mm, v(-38.1, -32.8) * mm, v(-38.45, -31.76) * mm]});
            skFitSpline(sketch, "E548", {"points": [v(-38.45, -31.76) * mm, v(-38.77, -30.72) * mm, v(-38.93, -29.41) * mm, v(-38.93, -27.82) * mm]});
            skFitSpline(sketch, "E549", {"points": [v(-27.67, -36.85) * mm, v(-27.14, -36.8) * mm, v(-26.63, -36.77) * mm, v(-26.16, -36.77) * mm]});
            skFitSpline(sketch, "E550", {"points": [v(-26.16, -36.77) * mm, v(-25.65, -36.77) * mm, v(-25.14, -36.8) * mm, v(-24.6, -36.85) * mm]});
            skFitSpline(sketch, "E551", {"points": [v(-24.6, -36.85) * mm, v(-24.63, -35.31) * mm, v(-24.66, -33.81) * mm, v(-24.68, -32.35) * mm]});
            skFitSpline(sketch, "E552", {"points": [v(-24.68, -32.35) * mm, v(-24.71, -30.9) * mm, v(-24.72, -29.25) * mm, v(-24.72, -27.42) * mm]});
            skFitSpline(sketch, "E553", {"points": [v(-24.72, -27.42) * mm, v(-24.72, -25.72) * mm, v(-24.71, -23.85) * mm, v(-24.68, -21.81) * mm]});
            skFitSpline(sketch, "E554", {"points": [v(-24.68, -21.81) * mm, v(-24.66, -19.77) * mm, v(-24.63, -17.78) * mm, v(-24.6, -15.84) * mm]});
            skFitSpline(sketch, "E555", {"points": [v(-24.6, -15.84) * mm, v(-24.55, -13.9) * mm, v(-24.5, -12.14) * mm, v(-24.45, -10.55) * mm]});
            skFitSpline(sketch, "E556", {"points": [v(-24.45, -10.55) * mm, v(-24.4, -8.93) * mm, v(-24.33, -7.7) * mm, v(-24.25, -6.85) * mm]});
            skFitSpline(sketch, "E557", {"points": [v(-24.25, -6.85) * mm, v(-24.6, -6.9) * mm, v(-24.9, -6.96) * mm, v(-25.2, -7.01) * mm]});
            skFitSpline(sketch, "E558", {"points": [v(-25.2, -7.01) * mm, v(-25.47, -7.04) * mm, v(-25.75, -7.05) * mm, v(-26.04, -7.05) * mm]});
            skFitSpline(sketch, "E559", {"points": [v(-26.04, -7.05) * mm, v(-26.33, -7.05) * mm, v(-26.62, -7.04) * mm, v(-26.91, -7.01) * mm]});
            skFitSpline(sketch, "E560", {"points": [v(-26.91, -7.01) * mm, v(-27.2, -6.96) * mm, v(-27.5, -6.9) * mm, v(-27.83, -6.85) * mm]});
            skFitSpline(sketch, "E561", {"points": [v(-27.83, -6.85) * mm, v(-27.8, -7.49) * mm, v(-27.79, -8.22) * mm, v(-27.79, -9.04) * mm]});
            skFitSpline(sketch, "E562", {"points": [v(-27.79, -9.04) * mm, v(-27.76, -9.86) * mm, v(-27.75, -10.74) * mm, v(-27.75, -11.67) * mm]});
            skFitSpline(sketch, "E563", {"points": [v(-27.75, -11.67) * mm, v(-27.72, -12.6) * mm, v(-27.7, -13.58) * mm, v(-27.7, -14.61) * mm]});
            skFitSpline(sketch, "E564", {"points": [v(-27.7, -14.61) * mm, v(-27.68, -15.62) * mm, v(-27.67, -16.63) * mm, v(-27.67, -17.63) * mm]});
            skFitSpline(sketch, "E565", {"points": [v(-27.75, -21.53) * mm, v(-28.89, -18.88) * mm, v(-30.93, -17.55) * mm, v(-33.87, -17.55) * mm]});
            skFitSpline(sketch, "E566", {"points": [v(-33.87, -17.55) * mm, v(-34.9, -17.55) * mm, v(-35.94, -17.77) * mm, v(-36.98, -18.2) * mm]});
            skFitSpline(sketch, "E567", {"points": [v(-36.98, -18.2) * mm, v(-37.99, -18.59) * mm, v(-38.9, -19.21) * mm, v(-39.72, -20.06) * mm]});
            skFitSpline(sketch, "E568", {"points": [v(-39.72, -20.06) * mm, v(-40.52, -20.88) * mm, v(-41.17, -21.92) * mm, v(-41.67, -23.16) * mm]});
            skFitSpline(sketch, "E569", {"points": [v(-41.67, -23.16) * mm, v(-42.18, -24.41) * mm, v(-42.43, -25.88) * mm, v(-42.43, -27.58) * mm]});
            skFitSpline(sketch, "E570", {"points": [v(-42.43, -27.58) * mm, v(-42.43, -29.3) * mm, v(-42.2, -30.8) * mm, v(-41.75, -32.04) * mm]});
            skFitSpline(sketch, "E571", {"points": [v(-41.75, -32.04) * mm, v(-41.27, -33.26) * mm, v(-40.66, -34.26) * mm, v(-39.92, -35.06) * mm]});
            skFitSpline(sketch, "E572", {"points": [v(-39.92, -35.06) * mm, v(-39.15, -35.83) * mm, v(-38.3, -36.39) * mm, v(-37.34, -36.73) * mm]});
            skFitSpline(sketch, "E573", {"points": [v(-37.34, -36.73) * mm, v(-36.35, -37.08) * mm, v(-35.36, -37.25) * mm, v(-34.35, -37.25) * mm]});
            skFitSpline(sketch, "E574", {"points": [v(-34.35, -37.25) * mm, v(-33.37, -37.25) * mm, v(-32.5, -37.12) * mm, v(-31.77, -36.85) * mm]});
            skFitSpline(sketch, "E575", {"points": [v(-31.77, -36.85) * mm, v(-31.02, -36.59) * mm, v(-30.39, -36.24) * mm, v(-29.86, -35.82) * mm]});
            skFitSpline(sketch, "E576", {"points": [v(-29.86, -35.82) * mm, v(-29.3, -35.4) * mm, v(-28.85, -34.94) * mm, v(-28.5, -34.46) * mm]});
            skFitSpline(sketch, "E577", {"points": [v(-28.5, -34.46) * mm, v(-28.13, -33.96) * mm, v(-27.84, -33.5) * mm, v(-27.63, -33.07) * mm]});
            skFitSpline(sketch, "E578", {"points": [v(-17.75, -27.1) * mm, v(-17.75, -27.72) * mm, v(-17.52, -28.23) * mm, v(-17.07, -28.66) * mm]});
            skFitSpline(sketch, "E579", {"points": [v(-17.07, -28.66) * mm, v(-16.62, -29.06) * mm, v(-16.09, -29.25) * mm, v(-15.48, -29.25) * mm]});
            skFitSpline(sketch, "E580", {"points": [v(-15.48, -29.25) * mm, v(-14.87, -29.25) * mm, v(-14.34, -29.06) * mm, v(-13.89, -28.66) * mm]});
            skFitSpline(sketch, "E581", {"points": [v(-13.89, -28.66) * mm, v(-13.44, -28.23) * mm, v(-13.21, -27.72) * mm, v(-13.21, -27.1) * mm]});
            skFitSpline(sketch, "E582", {"points": [v(-13.21, -27.1) * mm, v(-13.21, -26.5) * mm, v(-13.44, -25.97) * mm, v(-13.89, -25.51) * mm]});
            skFitSpline(sketch, "E583", {"points": [v(-13.89, -25.51) * mm, v(-14.34, -25.06) * mm, v(-14.87, -24.84) * mm, v(-15.48, -24.84) * mm]});
            skFitSpline(sketch, "E584", {"points": [v(-15.48, -24.84) * mm, v(-16.09, -24.84) * mm, v(-16.62, -25.06) * mm, v(-17.07, -25.51) * mm]});
            skFitSpline(sketch, "E585", {"points": [v(-17.07, -25.51) * mm, v(-17.52, -25.97) * mm, v(-17.75, -26.5) * mm, v(-17.75, -27.1) * mm]});
            skFitSpline(sketch, "E586", {"points": [v(-8.3, -19.59) * mm, v(-8.3, -21.4) * mm, v(-8.03, -22.92) * mm, v(-7.47, -24.16) * mm]});
            skFitSpline(sketch, "E587", {"points": [v(-7.47, -24.16) * mm, v(-6.89, -25.4) * mm, v(-6.13, -26.43) * mm, v(-5.2, -27.23) * mm]});
            skFitSpline(sketch, "E588", {"points": [v(-5.2, -27.23) * mm, v(-4.27, -28) * mm, v(-3.24, -28.55) * mm, v(-2.1, -28.9) * mm]});
            skFitSpline(sketch, "E589", {"points": [v(-2.1, -28.9) * mm, v(-0.93, -29.21) * mm, v(0.22, -29.37) * mm, v(1.36, -29.37) * mm]});
            skFitSpline(sketch, "E590", {"points": [v(1.36, -29.37) * mm, v(2.64, -29.37) * mm, v(3.86, -29.15) * mm, v(5.02, -28.7) * mm]});
            skFitSpline(sketch, "E591", {"points": [v(5.02, -28.7) * mm, v(6.22, -28.25) * mm, v(7.21, -27.7) * mm, v(8, -27.07) * mm]});
            skFitSpline(sketch, "E592", {"points": [v(8, -27.07) * mm, v(8.03, -26.4) * mm, v(8.11, -25.75) * mm, v(8.25, -25.12) * mm]});
            skFitSpline(sketch, "E593", {"points": [v(8.05, -25) * mm, v(7.7, -25.4) * mm, v(7.3, -25.77) * mm, v(6.81, -26.11) * mm]});
            skFitSpline(sketch, "E594", {"points": [v(6.81, -26.11) * mm, v(6.36, -26.46) * mm, v(5.87, -26.76) * mm, v(5.34, -27.03) * mm]});
            skFitSpline(sketch, "E595", {"points": [v(5.34, -27.03) * mm, v(4.81, -27.27) * mm, v(4.27, -27.46) * mm, v(3.71, -27.62) * mm]});
            skFitSpline(sketch, "E596", {"points": [v(3.71, -27.62) * mm, v(3.15, -27.76) * mm, v(2.6, -27.82) * mm, v(2.08, -27.82) * mm]});
            skFitSpline(sketch, "E597", {"points": [v(2.08, -27.82) * mm, v(-0.18, -27.82) * mm, v(-1.89, -27.13) * mm, v(-3.05, -25.75) * mm]});
            skFitSpline(sketch, "E598", {"points": [v(-3.05, -25.75) * mm, v(-4.22, -24.35) * mm, v(-4.8, -22.28) * mm, v(-4.8, -19.55) * mm]});
            skFitSpline(sketch, "E599", {"points": [v(-4.8, -19.55) * mm, v(-4.8, -18.33) * mm, v(-4.68, -17.2) * mm, v(-4.45, -16.17) * mm]});
            skFitSpline(sketch, "E600", {"points": [v(-4.45, -16.17) * mm, v(-4.18, -15.1) * mm, v(-3.78, -14.19) * mm, v(-3.25, -13.42) * mm]});
            skFitSpline(sketch, "E601", {"points": [v(-3.25, -13.42) * mm, v(-2.7, -12.65) * mm, v(-2, -12.05) * mm, v(-1.14, -11.63) * mm]});
            skFitSpline(sketch, "E602", {"points": [v(-1.14, -11.63) * mm, v(-0.27, -11.18) * mm, v(0.77, -10.95) * mm, v(1.96, -10.95) * mm]});
            skFitSpline(sketch, "E603", {"points": [v(1.96, -10.95) * mm, v(2.6, -10.95) * mm, v(3.18, -11.06) * mm, v(3.71, -11.27) * mm]});
            skFitSpline(sketch, "E604", {"points": [v(3.71, -11.27) * mm, v(4.24, -11.46) * mm, v(4.72, -11.7) * mm, v(5.14, -12.03) * mm]});
            skFitSpline(sketch, "E605", {"points": [v(5.14, -12.03) * mm, v(5.6, -12.32) * mm, v(5.98, -12.65) * mm, v(6.3, -13.02) * mm]});
            skFitSpline(sketch, "E606", {"points": [v(6.3, -13.02) * mm, v(6.61, -13.37) * mm, v(6.87, -13.71) * mm, v(7.05, -14.06) * mm]});
            skFitSpline(sketch, "E607", {"points": [v(7.37, -14.06) * mm, v(7.48, -13.58) * mm, v(7.6, -13.13) * mm, v(7.73, -12.7) * mm]});
            skFitSpline(sketch, "E608", {"points": [v(7.73, -12.7) * mm, v(7.89, -12.25) * mm, v(8.06, -11.83) * mm, v(8.25, -11.43) * mm]});
            skFitSpline(sketch, "E609", {"points": [v(8.25, -11.43) * mm, v(7.74, -10.98) * mm, v(6.9, -10.58) * mm, v(5.74, -10.24) * mm]});
            skFitSpline(sketch, "E610", {"points": [v(5.74, -10.24) * mm, v(4.6, -9.87) * mm, v(3.3, -9.68) * mm, v(1.84, -9.68) * mm]});
            skFitSpline(sketch, "E611", {"points": [v(1.84, -9.68) * mm, v(0.57, -9.68) * mm, v(-0.68, -9.88) * mm, v(-1.9, -10.28) * mm]});
            skFitSpline(sketch, "E612", {"points": [v(-1.9, -10.28) * mm, v(-3.12, -10.65) * mm, v(-4.2, -11.24) * mm, v(-5.16, -12.07) * mm]});
            skFitSpline(sketch, "E613", {"points": [v(-5.16, -12.07) * mm, v(-6.1, -12.86) * mm, v(-6.85, -13.88) * mm, v(-7.43, -15.13) * mm]});
            skFitSpline(sketch, "E614", {"points": [v(-7.43, -15.13) * mm, v(-8.01, -16.38) * mm, v(-8.3, -17.86) * mm, v(-8.3, -19.59) * mm]});
            skFitSpline(sketch, "E615", {"points": [v(14.81, -19.59) * mm, v(14.81, -18.47) * mm, v(14.9, -17.4) * mm, v(15.09, -16.36) * mm]});
            skFitSpline(sketch, "E616", {"points": [v(15.09, -16.36) * mm, v(15.3, -15.33) * mm, v(15.65, -14.41) * mm, v(16.12, -13.62) * mm]});
            skFitSpline(sketch, "E617", {"points": [v(16.12, -13.62) * mm, v(16.6, -12.8) * mm, v(17.24, -12.15) * mm, v(18.03, -11.67) * mm]});
            skFitSpline(sketch, "E618", {"points": [v(18.03, -11.67) * mm, v(18.83, -11.2) * mm, v(19.8, -10.95) * mm, v(20.98, -10.95) * mm]});
            skFitSpline(sketch, "E619", {"points": [v(20.98, -10.95) * mm, v(22.14, -10.95) * mm, v(23.13, -11.2) * mm, v(23.92, -11.67) * mm]});
            skFitSpline(sketch, "E620", {"points": [v(23.92, -11.67) * mm, v(24.72, -12.15) * mm, v(25.35, -12.8) * mm, v(25.83, -13.62) * mm]});
            skFitSpline(sketch, "E621", {"points": [v(25.83, -13.62) * mm, v(26.3, -14.41) * mm, v(26.64, -15.33) * mm, v(26.83, -16.36) * mm]});
            skFitSpline(sketch, "E622", {"points": [v(26.83, -16.36) * mm, v(27.04, -17.4) * mm, v(27.14, -18.47) * mm, v(27.14, -19.59) * mm]});
            skFitSpline(sketch, "E623", {"points": [v(27.14, -19.59) * mm, v(27.14, -20.7) * mm, v(27.04, -21.77) * mm, v(26.83, -22.8) * mm]});
            skFitSpline(sketch, "E624", {"points": [v(26.83, -22.8) * mm, v(26.64, -23.84) * mm, v(26.3, -24.77) * mm, v(25.83, -25.6) * mm]});
            skFitSpline(sketch, "E625", {"points": [v(25.83, -25.6) * mm, v(25.35, -26.39) * mm, v(24.72, -27.03) * mm, v(23.92, -27.5) * mm]});
            skFitSpline(sketch, "E626", {"points": [v(23.92, -27.5) * mm, v(23.13, -27.98) * mm, v(22.14, -28.22) * mm, v(20.98, -28.22) * mm]});
            skFitSpline(sketch, "E627", {"points": [v(20.98, -28.22) * mm, v(19.8, -28.22) * mm, v(18.83, -27.98) * mm, v(18.03, -27.5) * mm]});
            skFitSpline(sketch, "E628", {"points": [v(18.03, -27.5) * mm, v(17.24, -27.03) * mm, v(16.6, -26.39) * mm, v(16.12, -25.6) * mm]});
            skFitSpline(sketch, "E629", {"points": [v(16.12, -25.6) * mm, v(15.65, -24.77) * mm, v(15.3, -23.84) * mm, v(15.09, -22.8) * mm]});
            skFitSpline(sketch, "E630", {"points": [v(15.09, -22.8) * mm, v(14.9, -21.77) * mm, v(14.81, -20.7) * mm, v(14.81, -19.59) * mm]});
            skFitSpline(sketch, "E631", {"points": [v(11.3, -19.59) * mm, v(11.3, -21.4) * mm, v(11.59, -22.93) * mm, v(12.14, -24.2) * mm]});
            skFitSpline(sketch, "E632", {"points": [v(12.14, -24.2) * mm, v(12.73, -25.45) * mm, v(13.48, -26.47) * mm, v(14.41, -27.27) * mm]});
            skFitSpline(sketch, "E633", {"points": [v(14.41, -27.27) * mm, v(15.34, -28.03) * mm, v(16.38, -28.58) * mm, v(17.52, -28.9) * mm]});
            skFitSpline(sketch, "E634", {"points": [v(17.52, -28.9) * mm, v(18.68, -29.21) * mm, v(19.84, -29.37) * mm, v(20.98, -29.37) * mm]});
            skFitSpline(sketch, "E635", {"points": [v(20.98, -29.37) * mm, v(22.14, -29.37) * mm, v(23.3, -29.21) * mm, v(24.44, -28.9) * mm]});
            skFitSpline(sketch, "E636", {"points": [v(24.44, -28.9) * mm, v(25.58, -28.58) * mm, v(26.61, -28.03) * mm, v(27.54, -27.27) * mm]});
            skFitSpline(sketch, "E637", {"points": [v(27.54, -27.27) * mm, v(28.47, -26.47) * mm, v(29.21, -25.45) * mm, v(29.77, -24.2) * mm]});
            skFitSpline(sketch, "E638", {"points": [v(29.77, -24.2) * mm, v(30.35, -22.93) * mm, v(30.64, -21.4) * mm, v(30.64, -19.59) * mm]});
            skFitSpline(sketch, "E639", {"points": [v(30.64, -19.59) * mm, v(30.64, -17.78) * mm, v(30.35, -16.26) * mm, v(29.77, -15.01) * mm]});
            skFitSpline(sketch, "E640", {"points": [v(29.77, -15.01) * mm, v(29.21, -13.74) * mm, v(28.47, -12.72) * mm, v(27.54, -11.95) * mm]});
            skFitSpline(sketch, "E641", {"points": [v(27.54, -11.95) * mm, v(26.61, -11.15) * mm, v(25.58, -10.58) * mm, v(24.44, -10.24) * mm]});
            skFitSpline(sketch, "E642", {"points": [v(24.44, -10.24) * mm, v(23.3, -9.87) * mm, v(22.14, -9.68) * mm, v(20.98, -9.68) * mm]});
            skFitSpline(sketch, "E643", {"points": [v(20.98, -9.68) * mm, v(19.84, -9.68) * mm, v(18.68, -9.87) * mm, v(17.52, -10.24) * mm]});
            skFitSpline(sketch, "E644", {"points": [v(17.52, -10.24) * mm, v(16.38, -10.58) * mm, v(15.34, -11.15) * mm, v(14.41, -11.95) * mm]});
            skFitSpline(sketch, "E645", {"points": [v(14.41, -11.95) * mm, v(13.48, -12.72) * mm, v(12.73, -13.74) * mm, v(12.14, -15.01) * mm]});
            skFitSpline(sketch, "E646", {"points": [v(12.14, -15.01) * mm, v(11.59, -16.26) * mm, v(11.3, -17.78) * mm, v(11.3, -19.59) * mm]});
            skFitSpline(sketch, "E647", {"points": [v(35.17, -21.66) * mm, v(35.17, -22.85) * mm, v(35.14, -24.1) * mm, v(35.09, -25.43) * mm]});
            skFitSpline(sketch, "E648", {"points": [v(35.09, -25.43) * mm, v(35.06, -26.73) * mm, v(34.98, -27.91) * mm, v(34.85, -28.98) * mm]});
            skFitSpline(sketch, "E649", {"points": [v(34.85, -28.98) * mm, v(35.46, -28.92) * mm, v(36.05, -28.9) * mm, v(36.64, -28.9) * mm]});
            skFitSpline(sketch, "E650", {"points": [v(36.64, -28.9) * mm, v(37.22, -28.9) * mm, v(37.82, -28.92) * mm, v(38.43, -28.98) * mm]});
            skFitSpline(sketch, "E651", {"points": [v(38.43, -28.98) * mm, v(38.3, -27.91) * mm, v(38.2, -26.73) * mm, v(38.15, -25.43) * mm]});
            skFitSpline(sketch, "E652", {"points": [v(38.15, -25.43) * mm, v(38.12, -24.1) * mm, v(38.1, -22.85) * mm, v(38.1, -21.66) * mm]});
            skFitSpline(sketch, "E653", {"points": [v(38.1, -18.27) * mm, v(38.1, -16.2) * mm, v(38.52, -14.6) * mm, v(39.34, -13.46) * mm]});
            skFitSpline(sketch, "E654", {"points": [v(39.34, -13.46) * mm, v(40.17, -12.32) * mm, v(41.45, -11.75) * mm, v(43.2, -11.75) * mm]});
            skFitSpline(sketch, "E655", {"points": [v(43.2, -11.75) * mm, v(43.87, -11.75) * mm, v(44.5, -11.93) * mm, v(45.11, -12.3) * mm]});
            skFitSpline(sketch, "E656", {"points": [v(45.11, -12.3) * mm, v(45.75, -12.65) * mm, v(46.21, -13.08) * mm, v(46.5, -13.58) * mm]});
            skFitSpline(sketch, "E657", {"points": [v(46.5, -13.58) * mm, v(46.66, -13.9) * mm, v(46.78, -14.19) * mm, v(46.86, -14.45) * mm]});
            skFitSpline(sketch, "E658", {"points": [v(46.86, -14.45) * mm, v(46.97, -14.72) * mm, v(47.05, -15.06) * mm, v(47.1, -15.49) * mm]});
            skFitSpline(sketch, "E659", {"points": [v(47.1, -15.49) * mm, v(47.15, -15.89) * mm, v(47.18, -16.44) * mm, v(47.18, -17.16) * mm]});
            skFitSpline(sketch, "E660", {"points": [v(47.18, -17.16) * mm, v(47.2, -17.85) * mm, v(47.22, -18.82) * mm, v(47.22, -20.06) * mm]});
            skFitSpline(sketch, "E661", {"points": [v(47.22, -20.06) * mm, v(47.22, -21.52) * mm, v(47.2, -23) * mm, v(47.14, -24.52) * mm]});
            skFitSpline(sketch, "E662", {"points": [v(47.14, -24.52) * mm, v(47.09, -26.03) * mm, v(47, -27.52) * mm, v(46.86, -28.98) * mm]});
            skFitSpline(sketch, "E663", {"points": [v(46.86, -28.98) * mm, v(47.47, -28.92) * mm, v(48.06, -28.9) * mm, v(48.61, -28.9) * mm]});
            skFitSpline(sketch, "E664", {"points": [v(48.61, -28.9) * mm, v(49.17, -28.9) * mm, v(49.75, -28.92) * mm, v(50.36, -28.98) * mm]});
            skFitSpline(sketch, "E665", {"points": [v(50.36, -28.98) * mm, v(50.31, -27.86) * mm, v(50.26, -26.84) * mm, v(50.2, -25.91) * mm]});
            skFitSpline(sketch, "E666", {"points": [v(50.2, -25.91) * mm, v(50.18, -24.96) * mm, v(50.16, -23.9) * mm, v(50.16, -22.77) * mm]});
            skFitSpline(sketch, "E667", {"points": [v(50.16, -22.77) * mm, v(50.16, -20.89) * mm, v(50.18, -19.41) * mm, v(50.2, -18.35) * mm]});
            skFitSpline(sketch, "E668", {"points": [v(50.2, -18.35) * mm, v(50.23, -17.27) * mm, v(50.27, -16.43) * mm, v(50.32, -15.85) * mm]});
            skFitSpline(sketch, "E669", {"points": [v(50.32, -15.85) * mm, v(50.4, -15.24) * mm, v(50.5, -14.79) * mm, v(50.6, -14.5) * mm]});
            skFitSpline(sketch, "E670", {"points": [v(50.6, -14.5) * mm, v(50.73, -14.2) * mm, v(50.9, -13.91) * mm, v(51.12, -13.62) * mm]});
            skFitSpline(sketch, "E671", {"points": [v(51.12, -13.62) * mm, v(51.5, -13.11) * mm, v(52, -12.68) * mm, v(52.67, -12.3) * mm]});
            skFitSpline(sketch, "E672", {"points": [v(52.67, -12.3) * mm, v(53.33, -11.93) * mm, v(54.14, -11.75) * mm, v(55.1, -11.75) * mm]});
            skFitSpline(sketch, "E673", {"points": [v(55.1, -11.75) * mm, v(55.9, -11.75) * mm, v(56.56, -11.88) * mm, v(57.09, -12.15) * mm]});
            skFitSpline(sketch, "E674", {"points": [v(57.09, -12.15) * mm, v(57.62, -12.39) * mm, v(58.04, -12.72) * mm, v(58.36, -13.14) * mm]});
            skFitSpline(sketch, "E675", {"points": [v(58.36, -13.14) * mm, v(58.68, -13.57) * mm, v(58.9, -14.07) * mm, v(59.04, -14.65) * mm]});
            skFitSpline(sketch, "E676", {"points": [v(59.04, -14.65) * mm, v(59.2, -15.24) * mm, v(59.28, -15.86) * mm, v(59.28, -16.52) * mm]});
            skFitSpline(sketch, "E677", {"points": [v(59.28, -16.52) * mm, v(59.28, -20.13) * mm, v(59.22, -22.94) * mm, v(59.12, -24.96) * mm]});
            skFitSpline(sketch, "E678", {"points": [v(59.12, -24.96) * mm, v(59.04, -26.97) * mm, v(58.96, -28.31) * mm, v(58.88, -28.98) * mm]});
            skFitSpline(sketch, "E679", {"points": [v(58.88, -28.98) * mm, v(59.17, -28.92) * mm, v(59.46, -28.9) * mm, v(59.75, -28.9) * mm]});
            skFitSpline(sketch, "E680", {"points": [v(59.75, -28.9) * mm, v(60.04, -28.9) * mm, v(60.34, -28.9) * mm, v(60.63, -28.9) * mm]});
            skFitSpline(sketch, "E681", {"points": [v(60.63, -28.9) * mm, v(60.9, -28.9) * mm, v(61.17, -28.9) * mm, v(61.46, -28.9) * mm]});
            skFitSpline(sketch, "E682", {"points": [v(61.46, -28.9) * mm, v(61.76, -28.9) * mm, v(62.05, -28.92) * mm, v(62.34, -28.98) * mm]});
            skFitSpline(sketch, "E683", {"points": [v(62.34, -28.98) * mm, v(62.29, -28.2) * mm, v(62.25, -27.5) * mm, v(62.22, -26.83) * mm]});
            skFitSpline(sketch, "E684", {"points": [v(62.22, -26.83) * mm, v(62.22, -26.16) * mm, v(62.22, -25.47) * mm, v(62.22, -24.76) * mm]});
            skFitSpline(sketch, "E685", {"points": [v(62.22, -24.76) * mm, v(62.22, -23.6) * mm, v(62.23, -22.57) * mm, v(62.26, -21.7) * mm]});
            skFitSpline(sketch, "E686", {"points": [v(62.26, -21.7) * mm, v(62.29, -20.8) * mm, v(62.31, -20) * mm, v(62.34, -19.3) * mm]});
            skFitSpline(sketch, "E687", {"points": [v(62.34, -19.3) * mm, v(62.37, -18.6) * mm, v(62.4, -17.97) * mm, v(62.42, -17.44) * mm]});
            skFitSpline(sketch, "E688", {"points": [v(62.42, -17.44) * mm, v(62.44, -16.9) * mm, v(62.46, -16.42) * mm, v(62.46, -15.97) * mm]});
            skFitSpline(sketch, "E689", {"points": [v(62.46, -15.97) * mm, v(62.46, -14.85) * mm, v(62.3, -13.9) * mm, v(61.98, -13.1) * mm]});
            skFitSpline(sketch, "E690", {"points": [v(61.98, -13.1) * mm, v(61.69, -12.3) * mm, v(61.26, -11.66) * mm, v(60.7, -11.15) * mm]});
            skFitSpline(sketch, "E691", {"points": [v(60.7, -11.15) * mm, v(60.18, -10.65) * mm, v(59.54, -10.28) * mm, v(58.8, -10.04) * mm]});
            skFitSpline(sketch, "E692", {"points": [v(58.8, -10.04) * mm, v(58.06, -9.8) * mm, v(57.25, -9.68) * mm, v(56.37, -9.68) * mm]});
            skFitSpline(sketch, "E693", {"points": [v(56.37, -9.68) * mm, v(54.94, -9.68) * mm, v(53.67, -10.02) * mm, v(52.55, -10.71) * mm]});
            skFitSpline(sketch, "E694", {"points": [v(52.55, -10.71) * mm, v(51.46, -11.38) * mm, v(50.6, -12.35) * mm, v(49.97, -13.62) * mm]});
            skFitSpline(sketch, "E695", {"points": [v(49.89, -13.62) * mm, v(49.75, -13.06) * mm, v(49.5, -12.54) * mm, v(49.13, -12.07) * mm]});
            skFitSpline(sketch, "E696", {"points": [v(49.13, -12.07) * mm, v(48.76, -11.56) * mm, v(48.3, -11.14) * mm, v(47.78, -10.8) * mm]});
            skFitSpline(sketch, "E697", {"points": [v(47.78, -10.8) * mm, v(47.27, -10.45) * mm, v(46.7, -10.18) * mm, v(46.07, -10) * mm]});
            skFitSpline(sketch, "E698", {"points": [v(46.07, -10) * mm, v(45.43, -9.79) * mm, v(44.78, -9.68) * mm, v(44.12, -9.68) * mm]});
            skFitSpline(sketch, "E699", {"points": [v(44.12, -9.68) * mm, v(41.57, -9.68) * mm, v(39.6, -10.87) * mm, v(38.19, -13.26) * mm]});
            skFitSpline(sketch, "E700", {"points": [v(38.1, -13.26) * mm, v(38.1, -12.2) * mm, v(38.15, -11.14) * mm, v(38.23, -10.08) * mm]});
            skFitSpline(sketch, "E701", {"points": [v(38.23, -10.08) * mm, v(37.88, -10.13) * mm, v(37.58, -10.18) * mm, v(37.31, -10.24) * mm]});
            skFitSpline(sketch, "E702", {"points": [v(37.31, -10.24) * mm, v(37.08, -10.26) * mm, v(36.85, -10.28) * mm, v(36.64, -10.28) * mm]});
            skFitSpline(sketch, "E703", {"points": [v(36.64, -10.28) * mm, v(36.19, -10.28) * mm, v(35.6, -10.21) * mm, v(34.85, -10.08) * mm]});
            skFitSpline(sketch, "E704", {"points": [v(34.85, -10.08) * mm, v(34.98, -11.22) * mm, v(35.06, -12.45) * mm, v(35.09, -13.78) * mm]});
            skFitSpline(sketch, "E705", {"points": [v(35.09, -13.78) * mm, v(35.14, -15.08) * mm, v(35.17, -16.32) * mm, v(35.17, -17.52) * mm]});
            skSolve(sketch);
        }
        {
            var Q0;
            Q0=makeQuery(id+"F0.imprint","IMPRINT",FACE,{"disambiguationData":[TD([[makeQuery(id+"F0.imprint","IMPRINT",EDGE,{"derivedFrom":sQuery(id+"F0.wireOp",EDGE,"E87")}),1.0]])]});
            var Q1;
            Q1=makeQuery(id+"F0.imprint","IMPRINT",FACE,{"disambiguationData":[TD([[makeQuery(id+"F0.imprint","IMPRINT",EDGE,{"derivedFrom":sQuery(id+"F0.wireOp",EDGE,"E125")}),1.0]])]});
            var Q2;
            Q2=makeQuery(id+"F0.imprint","IMPRINT",FACE,{"disambiguationData":[TD([[makeQuery(id+"F0.imprint","IMPRINT",EDGE,{"derivedFrom":sQuery(id+"F0.wireOp",EDGE,"E163")}),1.0]])]});
            var Q3;
            Q3=makeQuery(id+"F0.imprint","IMPRINT",FACE,{"disambiguationData":[TD([[makeQuery(id+"F0.imprint","IMPRINT",EDGE,{"derivedFrom":sQuery(id+"F0.wireOp",EDGE,"E201")}),1.0]])]});
            var Q4;
            Q4=makeQuery(id+"F0.imprint","IMPRINT",FACE,{"disambiguationData":[TD([[makeQuery(id+"F0.imprint","IMPRINT",EDGE,{"derivedFrom":sQuery(id+"F0.wireOp",EDGE,"E1")}),-1.0]])]});
            var Q5;
            Q5=makeQuery(id+"F0.imprint","IMPRINT",FACE,{"disambiguationData":[TD([[makeQuery(id+"F0.imprint","IMPRINT",EDGE,{"derivedFrom":sQuery(id+"F0.wireOp",EDGE,"E5")}),-1.0]])]});
            var Q6;
            Q6=makeQuery(id+"F0.imprint","IMPRINT",FACE,{"disambiguationData":[TD([[makeQuery(id+"F0.imprint","IMPRINT",EDGE,{"derivedFrom":sQuery(id+"F0.wireOp",EDGE,"E18")}),-1.0]])]});
            var Q7;
            Q7=makeQuery(id+"F0.imprint","IMPRINT",FACE,{"disambiguationData":[TD([[makeQuery(id+"F0.imprint","IMPRINT",EDGE,{"derivedFrom":sQuery(id+"F0.wireOp",EDGE,"E286")}),1.0]])]});
            var Q8;
            Q8=makeQuery(id+"F0.imprint","IMPRINT",FACE,{"disambiguationData":[TD([[makeQuery(id+"F0.imprint","IMPRINT",EDGE,{"derivedFrom":sQuery(id+"F0.wireOp",EDGE,"E22")}),-1.0]])]});
            var Q9;
            Q9=makeQuery(id+"F0.imprint","IMPRINT",FACE,{"disambiguationData":[TD([[makeQuery(id+"F0.imprint","IMPRINT",EDGE,{"derivedFrom":sQuery(id+"F0.wireOp",EDGE,"E26")}),-1.0]])]});
            var Q10;
            Q10=makeQuery(id+"F0.imprint","IMPRINT",FACE,{"disambiguationData":[TD([[makeQuery(id+"F0.imprint","IMPRINT",EDGE,{"derivedFrom":sQuery(id+"F0.wireOp",EDGE,"E30")}),-1.0]])]});
            var Q11;
            Q11=makeQuery(id+"F0.imprint","IMPRINT",FACE,{"disambiguationData":[TD([[makeQuery(id+"F0.imprint","IMPRINT",EDGE,{"derivedFrom":sQuery(id+"F0.wireOp",EDGE,"E37")}),-1.0]])]});
            var Q12;
            Q12=makeQuery(id+"F0.imprint","IMPRINT",FACE,{"disambiguationData":[TD([[makeQuery(id+"F0.imprint","IMPRINT",EDGE,{"derivedFrom":sQuery(id+"F0.wireOp",EDGE,"E41")}),-1.0]])]});
            var Q13;
            Q13=makeQuery(id+"F0.imprint","IMPRINT",FACE,{"disambiguationData":[TD([[makeQuery(id+"F0.imprint","IMPRINT",EDGE,{"derivedFrom":sQuery(id+"F0.wireOp",EDGE,"E53")}),1.0]])]});
            var Q14;
            Q14=makeQuery(id+"F0.imprint","IMPRINT",FACE,{"disambiguationData":[TD([[makeQuery(id+"F0.imprint","IMPRINT",EDGE,{"derivedFrom":sQuery(id+"F0.wireOp",EDGE,"E59")}),-1.0]])]});
            var Q15;
            Q15=makeQuery(id+"F0.imprint","IMPRINT",FACE,{"disambiguationData":[TD([[makeQuery(id+"F0.imprint","IMPRINT",EDGE,{"derivedFrom":sQuery(id+"F0.wireOp",EDGE,"E69")}),-1.0]])]});
            var Q16;
            Q16=makeQuery(id+"F0.imprint","IMPRINT",FACE,{"disambiguationData":[TD([[makeQuery(id+"F0.imprint","IMPRINT",EDGE,{"derivedFrom":sQuery(id+"F0.wireOp",EDGE,"E578")}),1.0]])]});
            var Q17;
            Q17=makeQuery(id+"F0.imprint","IMPRINT",FACE,{"disambiguationData":[TD([[makeQuery(id+"F0.imprint","IMPRINT",EDGE,{"derivedFrom":sQuery(id+"F0.wireOp",EDGE,"E76")}),-1.0]])]});
            var Q18;
            Q18=makeQuery(id+"F0.imprint","IMPRINT",FACE,{"disambiguationData":[TD([[makeQuery(id+"F0.imprint","IMPRINT",EDGE,{"derivedFrom":sQuery(id+"F0.wireOp",EDGE,"E615")}),1.0]])]});
            var Q19;
            Q19=makeQuery(id+"F0.imprint","IMPRINT",FACE,{"disambiguationData":[TD([[makeQuery(id+"F0.imprint","IMPRINT",EDGE,{"derivedFrom":sQuery(id+"F0.wireOp",EDGE,"E80")}),-1.0]])]});
            extrude(context, id + "F1", {"entities" : qUnion([Q0, Q1, Q2, Q3, Q4, Q5, Q6, Q7, Q8, Q9, Q10, Q11, Q12, Q13, Q14, Q15, Q16, Q17, Q18, Q19]), "depth" : 2 * mm, "offsetDistance" : 25 * mm});
        }
    });
